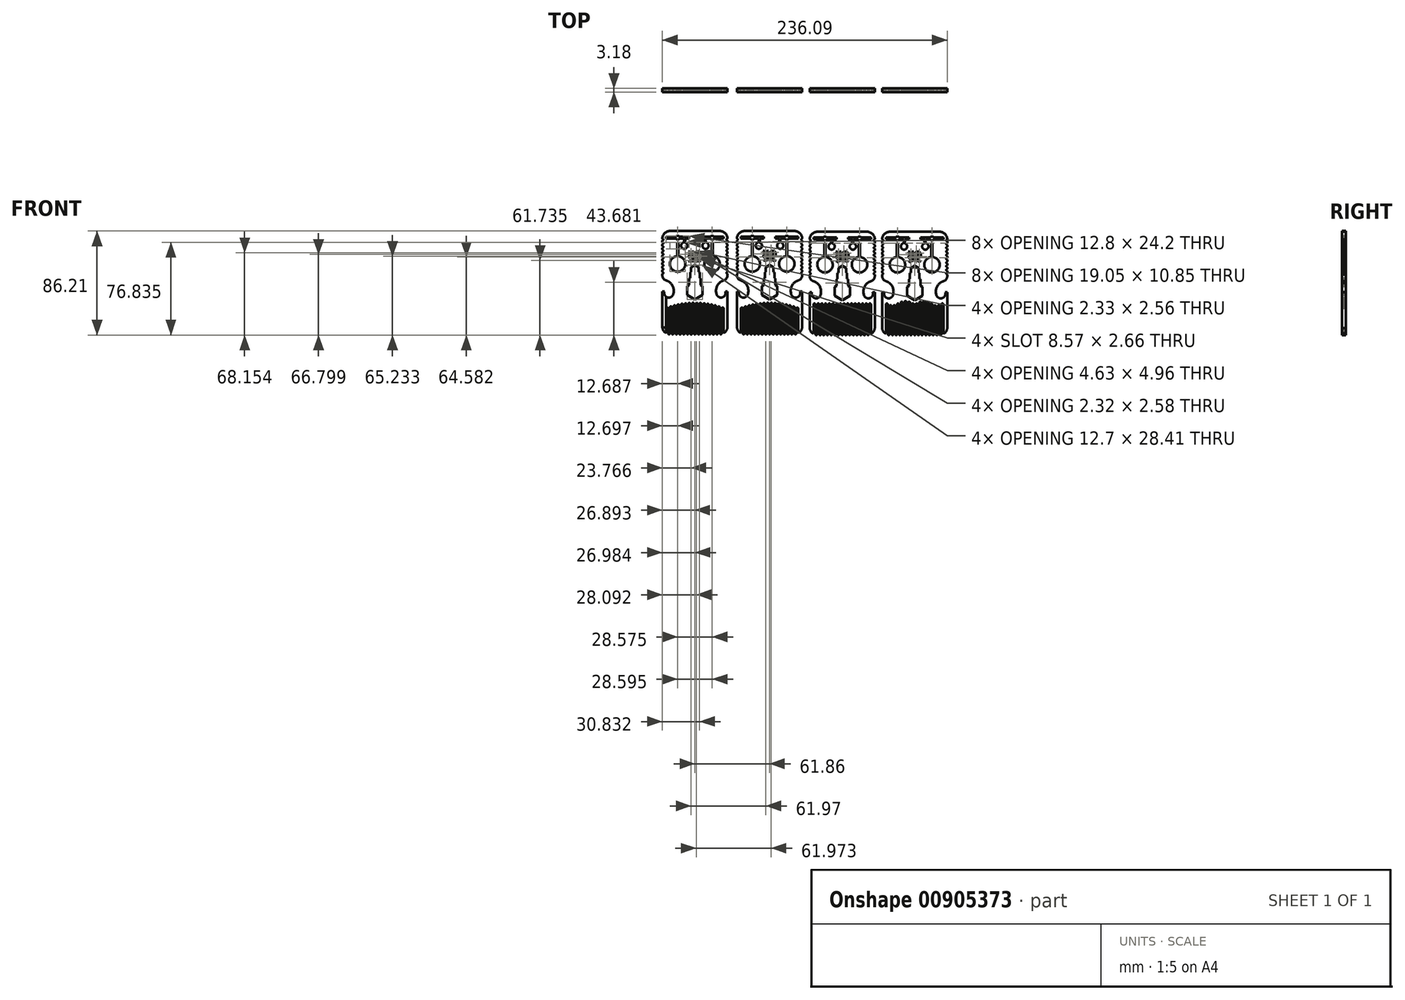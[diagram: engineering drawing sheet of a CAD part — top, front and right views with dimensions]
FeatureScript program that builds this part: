
annotation { "Feature Type Name" : "Feature", "Feature Type Description" : "" }
export const myFeature = defineFeature(function(context is Context, id is Id, definition is map)
    precondition{}
    {
        {
            var Q0;
            Q0=qCreatedBy(makeId("Front.planeOp"),FACE);
            var sketch = newSketch(context, id + "F0", { "sketchPlane" : qUnion([Q0])});
            skLineSegment(sketch, "E0.0", {"start": v(6.35, -8.3) * mm, "end": v(0, -11.96) * mm});
            skLineSegment(sketch, "E0.4", {"start": v(4.76, -0.05) * mm, "end": v(6.35, -0.97) * mm});
            skLineSegment(sketch, "E0.5", {"start": v(6.35, -0.97) * mm, "end": v(6.35, -8.3) * mm});
            skPoint(sketch, "E0.0.midPoint", {"position": v(3.17, -10.13) * mm});
            skLineSegment(sketch, "E1.4", {"start": v(3.97, 5.9) * mm, "end": v(4.76, 5.45) * mm});
            skLineSegment(sketch, "E1.5", {"start": v(4.76, 5.45) * mm, "end": v(4.76, -0.05) * mm});
            skPoint(sketch, "E2.visualSharp", {"position": v(-25.7, -41.44) * mm});
            skLineSegment(sketch, "E3.4", {"start": v(3.17, 10.95) * mm, "end": v(3.97, 10.5) * mm});
            skLineSegment(sketch, "E3.5", {"start": v(3.97, 10.5) * mm, "end": v(3.97, 5.9) * mm});
            skLineSegment(sketch, "E4.4", {"start": v(0, 16.45) * mm, "end": v(3.17, 14.61) * mm});
            skLineSegment(sketch, "E4.5", {"start": v(3.17, 14.61) * mm, "end": v(3.17, 10.95) * mm});
            skLineSegment(sketch, "E5.left", {"start": v(-26.99, 36.9) * mm, "end": v(-26.99, 35.36) * mm});
            skArc(sketch, "E6.filletArc", {"start": v(-20.64, 44.77) * mm, "mid": v(-25.13, 42.91) * mm, "end": v(-26.99, 38.42) * mm});
            skArc(sketch, "E7.filletArc", {"start": v(-26.95, -35.14) * mm, "mid": v(-26.28, -37.4) * mm, "end": v(-24.83, -39.24) * mm});
            skLineSegment(sketch, "E8", {"start": v(-23.81, 38.42) * mm, "end": v(-23.81, 40.01) * mm});
            skLineSegment(sketch, "E9", {"start": v(-23.81, 40.01) * mm, "end": v(-15.89, 40.01) * mm});
            skLineSegment(sketch, "E10", {"start": v(-4.76, 40.01) * mm, "end": v(-4.76, 38.42) * mm});
            skLineSegment(sketch, "E11", {"start": v(-23.81, 38.42) * mm, "end": v(-15.68, 38.42) * mm});
            skLineSegment(sketch, "E12.MirrorCS", {"start": v(-13.53, 27.58) * mm, "end": v(-13.53, 27.57) * mm});
            skLineSegment(sketch, "E13.MirrorCS", {"start": v(-15.06, 27.58) * mm, "end": v(-15.06, 27.57) * mm});
            skLineSegment(sketch, "E14.MirrorCS", {"start": v(-13.86, 35.24) * mm, "end": v(-14.75, 35.24) * mm});
            skLineSegment(sketch, "E15", {"start": v(-13.54, 23.8) * mm, "end": v(-13.53, 23.8) * mm});
            skLineSegment(sketch, "E16.0", {"start": v(-14.75, 35.24) * mm, "end": v(-14.75, 24.42) * mm});
            skLineSegment(sketch, "E17.0", {"start": v(-13.86, 35.24) * mm, "end": v(-13.86, 24.42) * mm});
            skArc(sketch, "E18", {"start": v(-15.3, 23.8) * mm, "mid": v(-14.28, 11.04) * mm, "end": v(-13.32, 23.8) * mm});
            skArc(sketch, "E19", {"start": v(-26.99, 9.3) * mm, "mid": v(-26.23, 10.07) * mm, "end": v(-26.99, 10.83) * mm});
            skArc(sketch, "E20", {"start": v(-26.99, 12.37) * mm, "mid": v(-26.23, 13.13) * mm, "end": v(-26.99, 13.9) * mm});
            skArc(sketch, "E21", {"start": v(-26.99, 15.43) * mm, "mid": v(-26.23, 16.2) * mm, "end": v(-26.99, 16.96) * mm});
            skArc(sketch, "E22", {"start": v(-26.99, 18.5) * mm, "mid": v(-26.23, 19.26) * mm, "end": v(-26.99, 20.03) * mm});
            skArc(sketch, "E23", {"start": v(-26.99, 21.56) * mm, "mid": v(-26.23, 22.33) * mm, "end": v(-26.99, 23.1) * mm});
            skArc(sketch, "E24", {"start": v(-26.99, 24.63) * mm, "mid": v(-26.23, 25.4) * mm, "end": v(-26.99, 26.16) * mm});
            skArc(sketch, "E25", {"start": v(-26.99, 27.7) * mm, "mid": v(-26.23, 28.46) * mm, "end": v(-26.99, 29.23) * mm});
            skArc(sketch, "E26", {"start": v(-26.99, 30.76) * mm, "mid": v(-26.23, 31.53) * mm, "end": v(-26.99, 32.3) * mm});
            skArc(sketch, "E27", {"start": v(-26.99, 33.83) * mm, "mid": v(-26.23, 34.6) * mm, "end": v(-26.99, 35.36) * mm});
            skArc(sketch, "E28", {"start": v(-26.99, 36.9) * mm, "mid": v(-26.23, 37.66) * mm, "end": v(-26.99, 38.42) * mm});
            skLineSegment(sketch, "E29.trimOffspring", {"start": v(-26.99, 12.37) * mm, "end": v(-26.99, 10.83) * mm});
            skLineSegment(sketch, "E30.trimOffspring", {"start": v(-26.99, 15.43) * mm, "end": v(-26.99, 13.9) * mm});
            skLineSegment(sketch, "E31.trimOffspring", {"start": v(-26.99, 18.5) * mm, "end": v(-26.99, 16.96) * mm});
            skLineSegment(sketch, "E32.trimOffspring", {"start": v(-26.99, 21.56) * mm, "end": v(-26.99, 20.03) * mm});
            skLineSegment(sketch, "E33.trimOffspring", {"start": v(-26.99, 24.63) * mm, "end": v(-26.99, 23.1) * mm});
            skLineSegment(sketch, "E34.trimOffspring", {"start": v(-26.99, 27.7) * mm, "end": v(-26.99, 26.16) * mm});
            skLineSegment(sketch, "E35.trimOffspring", {"start": v(-26.99, 30.76) * mm, "end": v(-26.99, 29.23) * mm});
            skLineSegment(sketch, "E36.trimOffspring", {"start": v(-26.99, 33.83) * mm, "end": v(-26.99, 32.3) * mm});
            skPoint(sketch, "E37.orphan", {"position": v(-14.3, 35.24) * mm});
            skLineSegment(sketch, "E38.trimOffspring", {"start": v(-12.71, 40.01) * mm, "end": v(-4.76, 40.01) * mm});
            skLineSegment(sketch, "E39", {"start": v(-15.89, 40.01) * mm, "end": v(-15.68, 40.01) * mm});
            skArc(sketch, "E40.MirrorCS", {"start": v(-15.68, 40.01) * mm, "mid": v(-14.29, 40.82) * mm, "end": v(-12.9, 40.01) * mm});
            skArc(sketch, "E41.MirrorCS", {"start": v(-12.9, 38.42) * mm, "mid": v(-14.29, 37.62) * mm, "end": v(-15.68, 38.42) * mm});
            skLineSegment(sketch, "E42.trimOffspring", {"start": v(-12.9, 38.42) * mm, "end": v(-9.28, 38.42) * mm});
            skLineSegment(sketch, "E43.trimOffspring", {"start": v(-12.9, 40.01) * mm, "end": v(-12.71, 40.01) * mm});
            skLineSegment(sketch, "E44.trimOffspring", {"start": v(-8.29, 38.42) * mm, "end": v(-4.76, 38.42) * mm});
            skArc(sketch, "E45", {"start": v(-9.9, 35.02) * mm, "mid": v(-8.95, 36.6) * mm, "end": v(-9.28, 38.42) * mm});
            skArc(sketch, "E46.0", {"start": v(-8.4, 35.5) * mm, "mid": v(-8.02, 36.95) * mm, "end": v(-8.29, 38.42) * mm});
            skPoint(sketch, "E47.start.orphan", {"position": v(-9.9, 35.02) * mm});
            skArc(sketch, "E48.MirrorCS", {"start": v(-9.9, 35.02) * mm, "mid": v(-8.58, 29.97) * mm, "end": v(-8.25, 35.18) * mm});
            skPoint(sketch, "E49.orphan", {"position": v(-9.94, 35) * mm});
            skArc(sketch, "E50", {"start": v(-15.3, 23.8) * mm, "mid": v(-14.92, 24.01) * mm, "end": v(-14.75, 24.42) * mm});
            skArc(sketch, "E51.MirrorCS", {"start": v(-13.3, 23.8) * mm, "mid": v(-13.69, 24.01) * mm, "end": v(-13.86, 24.42) * mm});
            skArc(sketch, "E52", {"start": v(-8.4, 35.5) * mm, "mid": v(-8.4, 35.3) * mm, "end": v(-8.25, 35.18) * mm});
            skLineSegment(sketch, "E53", {"start": v(-0.77, -40.07) * mm, "end": v(-0.77, -15.43) * mm});
            skArc(sketch, "E54", {"start": v(-0.77, -15.43) * mm, "mid": v(-1.53, -14.67) * mm, "end": v(-2.3, -15.43) * mm});
            skLineSegment(sketch, "E55", {"start": v(-2.3, -15.43) * mm, "end": v(-2.3, -40.07) * mm});
            skArc(sketch, "E56", {"start": v(-3.83, -40.07) * mm, "mid": v(-3.07, -40.82) * mm, "end": v(-2.3, -40.07) * mm});
            skLineSegment(sketch, "E57", {"start": v(-3.83, -40.07) * mm, "end": v(-3.83, -15.43) * mm});
            skArc(sketch, "E58", {"start": v(-3.83, -15.43) * mm, "mid": v(-4.6, -14.67) * mm, "end": v(-5.37, -15.43) * mm});
            skLineSegment(sketch, "E59", {"start": v(-5.37, -15.43) * mm, "end": v(-5.37, -40.07) * mm});
            skLineSegment(sketch, "E60", {"start": v(-6.9, -40.07) * mm, "end": v(-6.9, -15.43) * mm});
            skArc(sketch, "E61", {"start": v(-6.9, -15.43) * mm, "mid": v(-7.66, -14.67) * mm, "end": v(-8.43, -15.43) * mm});
            skLineSegment(sketch, "E62", {"start": v(-8.43, -15.43) * mm, "end": v(-8.43, -40.07) * mm});
            skArc(sketch, "E63", {"start": v(-6.9, -40.07) * mm, "mid": v(-6.13, -40.82) * mm, "end": v(-5.37, -40.07) * mm});
            skArc(sketch, "E64", {"start": v(-9.96, -40.07) * mm, "mid": v(-9.2, -40.82) * mm, "end": v(-8.43, -40.07) * mm});
            skLineSegment(sketch, "E65", {"start": v(-9.96, -40.07) * mm, "end": v(-9.96, -15.43) * mm});
            skArc(sketch, "E66", {"start": v(-9.96, -15.43) * mm, "mid": v(-10.73, -14.67) * mm, "end": v(-11.5, -15.43) * mm});
            skLineSegment(sketch, "E67", {"start": v(-11.5, -15.43) * mm, "end": v(-11.5, -40.07) * mm});
            skArc(sketch, "E68", {"start": v(-13.03, -40.07) * mm, "mid": v(-12.26, -40.82) * mm, "end": v(-11.5, -40.07) * mm});
            skLineSegment(sketch, "E69", {"start": v(-13.03, -40.07) * mm, "end": v(-13.03, -15.43) * mm});
            skArc(sketch, "E70", {"start": v(-13.03, -15.43) * mm, "mid": v(-13.8, -14.67) * mm, "end": v(-14.56, -15.43) * mm});
            skLineSegment(sketch, "E71", {"start": v(-14.56, -15.43) * mm, "end": v(-14.56, -40.07) * mm});
            skArc(sketch, "E72", {"start": v(-16.1, -40.07) * mm, "mid": v(-15.33, -40.82) * mm, "end": v(-14.56, -40.07) * mm});
            skLineSegment(sketch, "E73", {"start": v(-16.1, -40.07) * mm, "end": v(-16.1, -15.43) * mm});
            skArc(sketch, "E74", {"start": v(-16.1, -15.43) * mm, "mid": v(-16.86, -14.67) * mm, "end": v(-17.63, -15.43) * mm});
            skLineSegment(sketch, "E75", {"start": v(-17.63, -15.43) * mm, "end": v(-17.63, -40.07) * mm});
            skArc(sketch, "E76", {"start": v(-19.16, -40.07) * mm, "mid": v(-18.4, -40.82) * mm, "end": v(-17.63, -40.07) * mm});
            skLineSegment(sketch, "E77", {"start": v(-19.16, -40.07) * mm, "end": v(-19.16, -15.43) * mm});
            skArc(sketch, "E78", {"start": v(-19.16, -15.43) * mm, "mid": v(-19.93, -14.67) * mm, "end": v(-20.7, -15.43) * mm});
            skLineSegment(sketch, "E79", {"start": v(-20.7, -15.43) * mm, "end": v(-20.7, -40.02) * mm});
            skArc(sketch, "E80", {"start": v(-22.23, -40.01) * mm, "mid": v(-21.46, -40.77) * mm, "end": v(-20.7, -40.01) * mm});
            skLineSegment(sketch, "E81", {"start": v(-22.23, -40.01) * mm, "end": v(-22.23, -15.43) * mm});
            skArc(sketch, "E82", {"start": v(-22.23, -15.43) * mm, "mid": v(-23, -14.67) * mm, "end": v(-23.76, -15.43) * mm});
            skLineSegment(sketch, "E83", {"start": v(-23.76, -15.43) * mm, "end": v(-23.76, -38.74) * mm});
            skArc(sketch, "E84", {"start": v(-23.99, -39.27) * mm, "mid": v(-23.82, -39.03) * mm, "end": v(-23.76, -38.74) * mm});
            skArc(sketch, "E85", {"start": v(-0.77, -40.07) * mm, "mid": v(0, -40.82) * mm, "end": v(0.77, -40.07) * mm});
            skArc(sketch, "E86", {"start": v(2.3, -15.43) * mm, "mid": v(1.53, -14.67) * mm, "end": v(0.77, -15.43) * mm});
            skLineSegment(sketch, "E87.trimOffspring", {"start": v(-23.76, -40) * mm, "end": v(-23.76, -40.07) * mm});
            skArc(sketch, "E88", {"start": v(-24.83, -39.24) * mm, "mid": v(-24.41, -39.4) * mm, "end": v(-23.99, -39.27) * mm});
            skArc(sketch, "E89.MirrorCS", {"start": v(-26.98, 7.98) * mm, "mid": v(-26.1, 5.37) * mm, "end": v(-23.85, 3.81) * mm});
            skArc(sketch, "E90.MirrorCS", {"start": v(-20.94, 2.36) * mm, "mid": v(-22.34, 3.19) * mm, "end": v(-23.85, 3.81) * mm});
            skArc(sketch, "E91.MirrorCS", {"start": v(-17.92, -7.48) * mm, "mid": v(-17.94, -2.1) * mm, "end": v(-20.94, 2.36) * mm});
            skArc(sketch, "E92.MirrorCS", {"start": v(-25.18, -5.22) * mm, "mid": v(-22.75, -10.22) * mm, "end": v(-17.92, -7.48) * mm});
            skLineSegment(sketch, "E93.MirrorCS", {"start": v(-25.18, -5.22) * mm, "end": v(-26.98, -5.22) * mm});
            skLineSegment(sketch, "E94.MirrorCS", {"start": v(-26.98, -5.22) * mm, "end": v(-26.95, -35.14) * mm});
            skLineSegment(sketch, "E95", {"start": v(-26.98, 7.98) * mm, "end": v(-26.99, 9.3) * mm});
            skArc(sketch, "E96.MirrorCS", {"start": v(20.64, 44.77) * mm, "mid": v(25.13, 42.91) * mm, "end": v(26.99, 38.42) * mm});
            skLineSegment(sketch, "E97.MirrorCS", {"start": v(23.81, 40.01) * mm, "end": v(15.89, 40.01) * mm});
            skArc(sketch, "E98.MirrorCS", {"start": v(15.68, 40.01) * mm, "mid": v(14.29, 40.82) * mm, "end": v(12.9, 40.01) * mm});
            skLineSegment(sketch, "E99.MirrorCS", {"start": v(12.71, 40.01) * mm, "end": v(4.76, 40.01) * mm});
            skLineSegment(sketch, "E100.MirrorCS", {"start": v(4.76, 40.01) * mm, "end": v(4.76, 38.42) * mm});
            skLineSegment(sketch, "E101.MirrorCS", {"start": v(8.29, 38.42) * mm, "end": v(4.76, 38.42) * mm});
            skArc(sketch, "E102.MirrorCS", {"start": v(8.4, 35.5) * mm, "mid": v(8.02, 36.95) * mm, "end": v(8.29, 38.42) * mm});
            skLineSegment(sketch, "E103.MirrorCS", {"start": v(13.86, 35.24) * mm, "end": v(13.86, 24.42) * mm});
            skLineSegment(sketch, "E104.MirrorCS", {"start": v(14.75, 35.24) * mm, "end": v(14.75, 24.42) * mm});
            skLineSegment(sketch, "E105.MirrorCS", {"start": v(13.86, 35.24) * mm, "end": v(14.75, 35.24) * mm});
            skLineSegment(sketch, "E106.MirrorCS", {"start": v(12.9, 38.42) * mm, "end": v(9.28, 38.42) * mm});
            skArc(sketch, "E107.MirrorCS", {"start": v(12.9, 38.42) * mm, "mid": v(14.29, 37.62) * mm, "end": v(15.68, 38.42) * mm});
            skLineSegment(sketch, "E108.MirrorCS", {"start": v(23.81, 38.42) * mm, "end": v(15.68, 38.42) * mm});
            skLineSegment(sketch, "E109.MirrorCS", {"start": v(23.81, 38.42) * mm, "end": v(23.81, 40.01) * mm});
            skArc(sketch, "E110.MirrorCS", {"start": v(9.9, 35.02) * mm, "mid": v(8.95, 36.6) * mm, "end": v(9.28, 38.42) * mm});
            skArc(sketch, "E111.MirrorCS", {"start": v(9.9, 35.02) * mm, "mid": v(8.58, 29.97) * mm, "end": v(8.25, 35.18) * mm});
            skArc(sketch, "E112.MirrorCS", {"start": v(8.4, 35.5) * mm, "mid": v(8.4, 35.3) * mm, "end": v(8.25, 35.18) * mm});
            skLineSegment(sketch, "E113.MirrorCS", {"start": v(26.98, 7.98) * mm, "end": v(26.99, 9.3) * mm});
            skArc(sketch, "E114.MirrorCS", {"start": v(26.99, 33.83) * mm, "mid": v(26.23, 34.6) * mm, "end": v(26.99, 35.36) * mm});
            skLineSegment(sketch, "E115.MirrorCS", {"start": v(26.99, 33.83) * mm, "end": v(26.99, 32.3) * mm});
            skArc(sketch, "E116.MirrorCS", {"start": v(26.99, 9.3) * mm, "mid": v(26.23, 10.07) * mm, "end": v(26.99, 10.83) * mm});
            skArc(sketch, "E117.MirrorCS", {"start": v(26.99, 27.7) * mm, "mid": v(26.23, 28.46) * mm, "end": v(26.99, 29.23) * mm});
            skLineSegment(sketch, "E118.MirrorCS", {"start": v(26.99, 36.9) * mm, "end": v(26.99, 35.36) * mm});
            skLineSegment(sketch, "E119.MirrorCS", {"start": v(26.99, 15.43) * mm, "end": v(26.99, 13.9) * mm});
            skLineSegment(sketch, "E120.MirrorCS", {"start": v(26.99, 24.63) * mm, "end": v(26.99, 23.1) * mm});
            skLineSegment(sketch, "E121.MirrorCS", {"start": v(26.99, 21.56) * mm, "end": v(26.99, 20.03) * mm});
            skLineSegment(sketch, "E122.MirrorCS", {"start": v(26.99, 18.5) * mm, "end": v(26.99, 16.96) * mm});
            skArc(sketch, "E123.MirrorCS", {"start": v(26.99, 30.76) * mm, "mid": v(26.23, 31.53) * mm, "end": v(26.99, 32.3) * mm});
            skArc(sketch, "E124.MirrorCS", {"start": v(26.99, 21.56) * mm, "mid": v(26.23, 22.33) * mm, "end": v(26.99, 23.1) * mm});
            skLineSegment(sketch, "E125.MirrorCS", {"start": v(26.99, 30.76) * mm, "end": v(26.99, 29.23) * mm});
            skArc(sketch, "E126.MirrorCS", {"start": v(26.99, 24.63) * mm, "mid": v(26.23, 25.4) * mm, "end": v(26.99, 26.16) * mm});
            skArc(sketch, "E127.MirrorCS", {"start": v(26.99, 36.9) * mm, "mid": v(26.23, 37.66) * mm, "end": v(26.99, 38.42) * mm});
            skLineSegment(sketch, "E128.MirrorCS", {"start": v(26.99, 12.37) * mm, "end": v(26.99, 10.83) * mm});
            skLineSegment(sketch, "E129.MirrorCS", {"start": v(26.99, 27.7) * mm, "end": v(26.99, 26.16) * mm});
            skArc(sketch, "E130.MirrorCS", {"start": v(26.99, 15.43) * mm, "mid": v(26.23, 16.2) * mm, "end": v(26.99, 16.96) * mm});
            skArc(sketch, "E131.MirrorCS", {"start": v(26.99, 12.37) * mm, "mid": v(26.23, 13.13) * mm, "end": v(26.99, 13.9) * mm});
            skArc(sketch, "E132.MirrorCS", {"start": v(26.99, 18.5) * mm, "mid": v(26.23, 19.26) * mm, "end": v(26.99, 20.03) * mm});
            skArc(sketch, "E133.MirrorCS", {"start": v(13.03, -40.07) * mm, "mid": v(12.26, -40.82) * mm, "end": v(11.5, -40.07) * mm});
            skArc(sketch, "E134.MirrorCS", {"start": v(19.16, -40.07) * mm, "mid": v(18.4, -40.82) * mm, "end": v(17.63, -40.07) * mm});
            skArc(sketch, "E135.MirrorCS", {"start": v(9.96, -40.07) * mm, "mid": v(9.2, -40.82) * mm, "end": v(8.43, -40.07) * mm});
            skArc(sketch, "E136.MirrorCS", {"start": v(6.9, -40.07) * mm, "mid": v(6.13, -40.82) * mm, "end": v(5.37, -40.07) * mm});
            skLineSegment(sketch, "E137.MirrorCS", {"start": v(13.54, 23.8) * mm, "end": v(13.53, 23.8) * mm});
            skArc(sketch, "E138.MirrorCS", {"start": v(0.77, -40.07) * mm, "mid": v(0, -40.82) * mm, "end": v(-0.77, -40.07) * mm});
            skArc(sketch, "E139.MirrorCS", {"start": v(0.77, -15.43) * mm, "mid": v(1.53, -14.67) * mm, "end": v(2.3, -15.43) * mm});
            skArc(sketch, "E140.MirrorCS", {"start": v(13.3, 23.8) * mm, "mid": v(13.69, 24.01) * mm, "end": v(13.86, 24.42) * mm});
            skArc(sketch, "E141.MirrorCS", {"start": v(15.3, 23.8) * mm, "mid": v(14.92, 24.01) * mm, "end": v(14.75, 24.42) * mm});
            skLineSegment(sketch, "E142.MirrorCS", {"start": v(23.76, -40) * mm, "end": v(23.76, -40.07) * mm});
            skArc(sketch, "E143.MirrorCS", {"start": v(22.23, -40.01) * mm, "mid": v(21.46, -40.77) * mm, "end": v(20.7, -40.01) * mm});
            skLineSegment(sketch, "E144.MirrorCS", {"start": v(12.9, 40.01) * mm, "end": v(12.71, 40.01) * mm});
            skArc(sketch, "E145.MirrorCS", {"start": v(3.83, -40.07) * mm, "mid": v(3.07, -40.82) * mm, "end": v(2.3, -40.07) * mm});
            skLineSegment(sketch, "E146.MirrorCS", {"start": v(15.89, 40.01) * mm, "end": v(15.68, 40.01) * mm});
            skArc(sketch, "E147.MirrorCS", {"start": v(16.1, -40.07) * mm, "mid": v(15.33, -40.82) * mm, "end": v(14.56, -40.07) * mm});
            skArc(sketch, "E148.MirrorCS", {"start": v(24.83, -39.24) * mm, "mid": v(24.41, -39.4) * mm, "end": v(23.99, -39.27) * mm});
            skLineSegment(sketch, "E149.MirrorCS", {"start": v(25.18, -5.22) * mm, "end": v(26.98, -5.22) * mm});
            skArc(sketch, "E150.MirrorCS", {"start": v(26.95, -35.14) * mm, "mid": v(26.28, -37.4) * mm, "end": v(24.83, -39.24) * mm});
            skLineSegment(sketch, "E151.MirrorCS", {"start": v(-3.18, 10.95) * mm, "end": v(-3.97, 10.5) * mm});
            skArc(sketch, "E152.MirrorCS", {"start": v(23.99, -39.27) * mm, "mid": v(23.82, -39.03) * mm, "end": v(23.76, -38.74) * mm});
            skLineSegment(sketch, "E153.MirrorCS", {"start": v(-3.97, 10.5) * mm, "end": v(-3.97, 5.9) * mm});
            skLineSegment(sketch, "E154.MirrorCS", {"start": v(-3.18, 14.61) * mm, "end": v(-3.18, 10.95) * mm});
            skLineSegment(sketch, "E155.MirrorCS", {"start": v(-3.97, 5.9) * mm, "end": v(-4.76, 5.45) * mm});
            skLineSegment(sketch, "E156.MirrorCS", {"start": v(13.53, 27.58) * mm, "end": v(13.53, 27.57) * mm});
            skLineSegment(sketch, "E157.MirrorCS", {"start": v(15.06, 27.58) * mm, "end": v(15.06, 27.57) * mm});
            skArc(sketch, "E158.MirrorCS", {"start": v(20.94, 2.36) * mm, "mid": v(22.34, 3.19) * mm, "end": v(23.85, 3.81) * mm});
            skLineSegment(sketch, "E159.MirrorCS", {"start": v(-4.76, -0.05) * mm, "end": v(-6.35, -0.97) * mm});
            skLineSegment(sketch, "E160.MirrorCS", {"start": v(0, 16.45) * mm, "end": v(-3.18, 14.61) * mm});
            skLineSegment(sketch, "E161.MirrorCS", {"start": v(-6.35, -8.3) * mm, "end": v(0, -11.96) * mm});
            skLineSegment(sketch, "E162.MirrorCS", {"start": v(17.63, -16.84) * mm, "end": v(17.63, -40.07) * mm});
            skLineSegment(sketch, "E163.MirrorCS", {"start": v(-6.35, -0.97) * mm, "end": v(-6.35, -8.3) * mm});
            skLineSegment(sketch, "E164.MirrorCS", {"start": v(11.5, -15.43) * mm, "end": v(11.5, -40.07) * mm});
            skLineSegment(sketch, "E165.MirrorCS", {"start": v(22.23, -40.01) * mm, "end": v(22.23, -15.43) * mm});
            skLineSegment(sketch, "E166.MirrorCS", {"start": v(26.98, -5.22) * mm, "end": v(26.95, -35.14) * mm});
            skArc(sketch, "E167.MirrorCS", {"start": v(17.92, -7.48) * mm, "mid": v(17.94, -2.1) * mm, "end": v(20.94, 2.36) * mm});
            skLineSegment(sketch, "E168.MirrorCS", {"start": v(23.76, -15.43) * mm, "end": v(23.76, -38.74) * mm});
            skPoint(sketch, "E169.MirrorP", {"position": v(14.3, 35.24) * mm});
            skArc(sketch, "E170.MirrorCS", {"start": v(25.18, -5.22) * mm, "mid": v(22.75, -10.22) * mm, "end": v(17.92, -7.48) * mm});
            skLineSegment(sketch, "E171.MirrorCS", {"start": v(0.77, -40.07) * mm, "end": v(0.77, -15.43) * mm});
            skPoint(sketch, "E172.MirrorP", {"position": v(-3.18, -10.13) * mm});
            skLineSegment(sketch, "E173.MirrorCS", {"start": v(16.1, -40.07) * mm, "end": v(16.1, -16.84) * mm});
            skPoint(sketch, "E174.MirrorP", {"position": v(26.99, -34.47) * mm});
            skPoint(sketch, "E175.MirrorP", {"position": v(9.9, 35.02) * mm});
            skLineSegment(sketch, "E176.MirrorCS", {"start": v(3.83, -40.07) * mm, "end": v(3.83, -15.43) * mm});
            skLineSegment(sketch, "E177.MirrorCS", {"start": v(14.56, -15.43) * mm, "end": v(14.56, -40.07) * mm});
            skArc(sketch, "E178.MirrorCS", {"start": v(15.3, 23.8) * mm, "mid": v(14.28, 11.04) * mm, "end": v(13.32, 23.8) * mm});
            skPoint(sketch, "E179.MirrorP", {"position": v(9.94, 35) * mm});
            skArc(sketch, "E180.MirrorCS", {"start": v(26.98, 7.98) * mm, "mid": v(26.1, 5.37) * mm, "end": v(23.85, 3.81) * mm});
            skLineSegment(sketch, "E181.MirrorCS", {"start": v(5.37, -15.43) * mm, "end": v(5.37, -40.07) * mm});
            skLineSegment(sketch, "E182.MirrorCS", {"start": v(-4.76, 5.45) * mm, "end": v(-4.76, -0.05) * mm});
            skLineSegment(sketch, "E183.MirrorCS", {"start": v(13.03, -40.07) * mm, "end": v(13.03, -15.43) * mm});
            skPoint(sketch, "E184.MirrorP", {"position": v(25.7, -41.44) * mm});
            skLineSegment(sketch, "E185.MirrorCS", {"start": v(19.16, -40.07) * mm, "end": v(19.16, -16.84) * mm});
            skLineSegment(sketch, "E186.MirrorCS", {"start": v(9.96, -40.07) * mm, "end": v(9.96, -15.43) * mm});
            skLineSegment(sketch, "E187.MirrorCS", {"start": v(8.43, -15.43) * mm, "end": v(8.43, -40.07) * mm});
            skLineSegment(sketch, "E188.MirrorCS", {"start": v(2.3, -15.43) * mm, "end": v(2.3, -40.07) * mm});
            skLineSegment(sketch, "E189.MirrorCS", {"start": v(6.9, -40.07) * mm, "end": v(6.9, -15.43) * mm});
            skLineSegment(sketch, "E190", {"start": v(-20.64, 44.77) * mm, "end": v(20.64, 44.77) * mm});
            skArc(sketch, "E191", {"start": v(4.3, 20.82) * mm, "mid": v(0, 22.07) * mm, "end": v(-4.26, 20.7) * mm});
            skArc(sketch, "E192", {"start": v(1.59, 27.05) * mm, "mid": v(1.34, 26.49) * mm, "end": v(1.22, 25.88) * mm});
            skArc(sketch, "E193", {"start": v(1.32, 24.9) * mm, "mid": v(1.68, 24.22) * mm, "end": v(2.39, 23.9) * mm});
            skArc(sketch, "E194", {"start": v(2.38, 28.44) * mm, "mid": v(2.03, 28.4) * mm, "end": v(1.69, 28.32) * mm});
            skArc(sketch, "E195", {"start": v(1.69, 28.32) * mm, "mid": v(1.26, 28.15) * mm, "end": v(0.88, 27.9) * mm});
            skArc(sketch, "E196", {"start": v(0.88, 27.9) * mm, "mid": v(0.52, 27.5) * mm, "end": v(0.28, 27.03) * mm});
            skArc(sketch, "E197", {"start": v(0.28, 27.03) * mm, "mid": v(0.11, 26.47) * mm, "end": v(0.05, 25.88) * mm});
            skArc(sketch, "E198", {"start": v(0.05, 25.88) * mm, "mid": v(0.05, 25.88) * mm, "end": v(0.05, 25.88) * mm});
            skArc(sketch, "E199", {"start": v(0.09, 25.07) * mm, "mid": v(0.16, 24.69) * mm, "end": v(0.28, 24.32) * mm});
            skArc(sketch, "E200", {"start": v(0.28, 24.32) * mm, "mid": v(0.42, 24.03) * mm, "end": v(0.6, 23.76) * mm});
            skArc(sketch, "E201", {"start": v(0.6, 23.76) * mm, "mid": v(0.86, 23.5) * mm, "end": v(1.16, 23.28) * mm});
            skArc(sketch, "E202", {"start": v(1.16, 23.28) * mm, "mid": v(1.5, 23.12) * mm, "end": v(1.87, 23.02) * mm});
            skArc(sketch, "E203", {"start": v(1.87, 23.02) * mm, "mid": v(2.1, 22.97) * mm, "end": v(2.35, 22.95) * mm});
            skArc(sketch, "E204", {"start": v(2.35, 22.95) * mm, "mid": v(2.37, 22.95) * mm, "end": v(2.39, 22.95) * mm});
            skLineSegment(sketch, "E205", {"start": v(2.58, 27.5) * mm, "end": v(2.58, 27.5) * mm});
            skLineSegment(sketch, "E206", {"start": v(2.59, 23.88) * mm, "end": v(2.59, 23.87) * mm});
            skLineSegment(sketch, "E207.trimOffspring", {"start": v(2.39, 27.47) * mm, "end": v(2.38, 28.44) * mm});
            skLineSegment(sketch, "E208", {"start": v(2.39, 23.42) * mm, "end": v(2.39, 22.95) * mm});
            skArc(sketch, "E209.trimOffspring", {"start": v(2.59, 22.94) * mm, "mid": v(2.6, 22.94) * mm, "end": v(2.6, 22.94) * mm});
            skLineSegment(sketch, "E210.trimOffspring", {"start": v(2.39, 23.9) * mm, "end": v(2.39, 23.42) * mm});
            skArc(sketch, "E211.trimOffspring", {"start": v(2.39, 27.47) * mm, "mid": v(1.95, 27.33) * mm, "end": v(1.59, 27.05) * mm});
            skPoint(sketch, "E212.orphan", {"position": v(1.21, 25.62) * mm});
            skArc(sketch, "E213.MirrorCS", {"start": v(2.77, 27.48) * mm, "mid": v(3.2, 27.34) * mm, "end": v(3.57, 27.06) * mm});
            skArc(sketch, "E214.MirrorCS", {"start": v(3.57, 27.06) * mm, "mid": v(3.82, 26.5) * mm, "end": v(3.94, 25.9) * mm});
            skArc(sketch, "E215.MirrorCS", {"start": v(3.86, 24.92) * mm, "mid": v(3.5, 24.23) * mm, "end": v(2.8, 23.9) * mm});
            skArc(sketch, "E216.MirrorCS", {"start": v(2.85, 22.95) * mm, "mid": v(2.83, 22.95) * mm, "end": v(2.8, 22.95) * mm});
            skArc(sketch, "E217.MirrorCS", {"start": v(3.32, 23.02) * mm, "mid": v(3.09, 22.98) * mm, "end": v(2.85, 22.95) * mm});
            skArc(sketch, "E218.MirrorCS", {"start": v(4.03, 23.3) * mm, "mid": v(3.69, 23.13) * mm, "end": v(3.32, 23.02) * mm});
            skArc(sketch, "E219.MirrorCS", {"start": v(4.58, 23.78) * mm, "mid": v(4.33, 23.52) * mm, "end": v(4.03, 23.3) * mm});
            skArc(sketch, "E220.MirrorCS", {"start": v(4.9, 24.34) * mm, "mid": v(4.76, 24.05) * mm, "end": v(4.58, 23.78) * mm});
            skArc(sketch, "E221.MirrorCS", {"start": v(5.08, 25.1) * mm, "mid": v(5.02, 24.71) * mm, "end": v(4.9, 24.34) * mm});
            skArc(sketch, "E222.MirrorCS", {"start": v(5.11, 25.9) * mm, "mid": v(5.11, 25.9) * mm, "end": v(5.11, 25.9) * mm});
            skArc(sketch, "E223.MirrorCS", {"start": v(4.88, 27.05) * mm, "mid": v(5.05, 26.5) * mm, "end": v(5.11, 25.9) * mm});
            skArc(sketch, "E224.MirrorCS", {"start": v(4.27, 27.9) * mm, "mid": v(4.63, 27.52) * mm, "end": v(4.88, 27.05) * mm});
            skArc(sketch, "E225.MirrorCS", {"start": v(3.45, 28.33) * mm, "mid": v(3.88, 28.16) * mm, "end": v(4.27, 27.9) * mm});
            skArc(sketch, "E226.MirrorCS", {"start": v(2.76, 28.44) * mm, "mid": v(3.11, 28.4) * mm, "end": v(3.45, 28.33) * mm});
            skLineSegment(sketch, "E227.MirrorCS", {"start": v(2.77, 27.48) * mm, "end": v(2.76, 28.44) * mm});
            skLineSegment(sketch, "E228.MirrorCS", {"start": v(2.8, 23.9) * mm, "end": v(2.8, 23.42) * mm});
            skLineSegment(sketch, "E229.MirrorCS", {"start": v(2.8, 23.42) * mm, "end": v(2.8, 22.95) * mm});
            skArc(sketch, "E230", {"start": v(2.59, 23.87) * mm, "mid": v(2.6, 23.87) * mm, "end": v(2.6, 23.87) * mm});
            skLineSegment(sketch, "E231.0", {"start": v(0.05, 25.5) * mm, "end": v(1.22, 25.5) * mm});
            skLineSegment(sketch, "E232.0", {"start": v(0.05, 25.88) * mm, "end": v(1.22, 25.88) * mm});
            skLineSegment(sketch, "E233.trimOffspring", {"start": v(3.94, 25.9) * mm, "end": v(5.12, 25.9) * mm});
            skPoint(sketch, "E234.orphan", {"position": v(2.58, 25.7) * mm});
            skLineSegment(sketch, "E235.trimOffspring", {"start": v(3.95, 25.52) * mm, "end": v(5.12, 25.53) * mm});
            skPoint(sketch, "E236.MirrorCS.end.orphan", {"position": v(2.6, 23.87) * mm});
            skPoint(sketch, "E236.MirrorCS.start.orphan", {"position": v(2.8, 23.9) * mm});
            skPoint(sketch, "E237.MirrorCS.end.orphan", {"position": v(2.98, 22.94) * mm});
            skPoint(sketch, "E237.MirrorCS.start.orphan", {"position": v(3.19, 22.95) * mm});
            skPoint(sketch, "E238.orphan", {"position": v(2.57, 28.44) * mm});
            skPoint(sketch, "E239.MirrorCS.end.orphan", {"position": v(2.77, 27.48) * mm});
            skArc(sketch, "E240.trimOffspring", {"start": v(0.05, 25.5) * mm, "mid": v(0.06, 25.29) * mm, "end": v(0.09, 25.07) * mm});
            skArc(sketch, "E241.trimOffspring", {"start": v(1.22, 25.5) * mm, "mid": v(1.25, 25.2) * mm, "end": v(1.32, 24.9) * mm});
            skArc(sketch, "E242.trimOffspring", {"start": v(3.95, 25.52) * mm, "mid": v(3.92, 25.22) * mm, "end": v(3.86, 24.92) * mm});
            skArc(sketch, "E243.trimOffspring", {"start": v(5.12, 25.53) * mm, "mid": v(5.1, 25.31) * mm, "end": v(5.08, 25.1) * mm});
            skText(sketch, "E244", { "text": "X", "fontName": "OpenSans-Bold.ttf"});
            skLineSegment(sketch, "E245", {"start": v(4.3, 19.56) * mm, "end": v(4.3, 20.82) * mm});
            skLineSegment(sketch, "E246", {"start": v(4.3, 20.82) * mm, "end": v(4.3, 19.56) * mm});
            skCircle(sketch, "E247", {"center": v(2.58, 25.7) * mm, "radius": 0.65 * mm});
            skArc(sketch, "E248.0", {"start": v(4.3, 19.56) * mm, "mid": v(0, 21.05) * mm, "end": v(-4.26, 19.4) * mm});
            skLineSegment(sketch, "E249", {"start": v(-4.26, 20.7) * mm, "end": v(-4.26, 19.4) * mm});
            skLineSegment(sketch, "E250.trimOffspring", {"start": v(20.7, -16.84) * mm, "end": v(20.7, -40.02) * mm});
            skLineSegment(sketch, "E251.0", {"start": v(66.38, -8.3) * mm, "end": v(60.03, -11.96) * mm});
            skLineSegment(sketch, "E251.4", {"start": v(64.8, -0.05) * mm, "end": v(66.38, -0.97) * mm});
            skLineSegment(sketch, "E251.5", {"start": v(66.38, -0.97) * mm, "end": v(66.38, -8.3) * mm});
            skPoint(sketch, "E251.0.midPoint", {"position": v(63.2, -10.13) * mm});
            skLineSegment(sketch, "E252.4", {"start": v(64, 5.9) * mm, "end": v(64.8, 5.45) * mm});
            skLineSegment(sketch, "E252.5", {"start": v(64.8, 5.45) * mm, "end": v(64.8, -0.05) * mm});
            skPoint(sketch, "E253.visualSharp", {"position": v(34.33, -41.44) * mm});
            skLineSegment(sketch, "E254.4", {"start": v(63.2, 10.95) * mm, "end": v(64, 10.5) * mm});
            skLineSegment(sketch, "E254.5", {"start": v(64, 10.5) * mm, "end": v(64, 5.9) * mm});
            skLineSegment(sketch, "E255.4", {"start": v(60.03, 16.45) * mm, "end": v(63.2, 14.61) * mm});
            skLineSegment(sketch, "E255.5", {"start": v(63.2, 14.61) * mm, "end": v(63.2, 10.95) * mm});
            skLineSegment(sketch, "E256.left", {"start": v(33.04, 36.9) * mm, "end": v(33.04, 35.36) * mm});
            skArc(sketch, "E257.filletArc", {"start": v(39.4, 44.77) * mm, "mid": v(34.9, 42.91) * mm, "end": v(33.04, 38.42) * mm});
            skArc(sketch, "E258.filletArc", {"start": v(33.08, -35.14) * mm, "mid": v(33.75, -37.4) * mm, "end": v(35.2, -39.24) * mm});
            skLineSegment(sketch, "E259", {"start": v(36.22, 38.42) * mm, "end": v(36.22, 40.01) * mm});
            skLineSegment(sketch, "E260", {"start": v(36.22, 40.01) * mm, "end": v(44.14, 40.01) * mm});
            skLineSegment(sketch, "E261", {"start": v(55.27, 40.01) * mm, "end": v(55.27, 38.42) * mm});
            skLineSegment(sketch, "E262", {"start": v(36.22, 38.42) * mm, "end": v(44.35, 38.42) * mm});
            skLineSegment(sketch, "E263.MirrorCS", {"start": v(46.5, 27.58) * mm, "end": v(46.5, 27.57) * mm});
            skLineSegment(sketch, "E264.MirrorCS", {"start": v(44.97, 27.58) * mm, "end": v(44.97, 27.57) * mm});
            skLineSegment(sketch, "E265.MirrorCS", {"start": v(46.17, 35.24) * mm, "end": v(45.28, 35.24) * mm});
            skLineSegment(sketch, "E266", {"start": v(46.49, 23.8) * mm, "end": v(46.5, 23.8) * mm});
            skLineSegment(sketch, "E267.0", {"start": v(45.28, 35.24) * mm, "end": v(45.28, 24.42) * mm});
            skLineSegment(sketch, "E268.0", {"start": v(46.17, 35.24) * mm, "end": v(46.17, 24.42) * mm});
            skArc(sketch, "E269", {"start": v(44.73, 23.8) * mm, "mid": v(45.75, 11.04) * mm, "end": v(46.71, 23.8) * mm});
            skArc(sketch, "E270", {"start": v(33.04, 9.3) * mm, "mid": v(33.8, 10.07) * mm, "end": v(33.04, 10.83) * mm});
            skArc(sketch, "E271", {"start": v(33.04, 12.37) * mm, "mid": v(33.8, 13.13) * mm, "end": v(33.04, 13.9) * mm});
            skArc(sketch, "E272", {"start": v(33.04, 15.43) * mm, "mid": v(33.8, 16.2) * mm, "end": v(33.04, 16.96) * mm});
            skArc(sketch, "E273", {"start": v(33.04, 18.5) * mm, "mid": v(33.8, 19.26) * mm, "end": v(33.04, 20.03) * mm});
            skArc(sketch, "E274", {"start": v(33.04, 21.56) * mm, "mid": v(33.8, 22.33) * mm, "end": v(33.04, 23.1) * mm});
            skArc(sketch, "E275", {"start": v(33.04, 24.63) * mm, "mid": v(33.8, 25.4) * mm, "end": v(33.04, 26.16) * mm});
            skArc(sketch, "E276", {"start": v(33.04, 27.7) * mm, "mid": v(33.8, 28.46) * mm, "end": v(33.04, 29.23) * mm});
            skArc(sketch, "E277", {"start": v(33.04, 30.76) * mm, "mid": v(33.8, 31.53) * mm, "end": v(33.04, 32.3) * mm});
            skArc(sketch, "E278", {"start": v(33.04, 33.83) * mm, "mid": v(33.8, 34.6) * mm, "end": v(33.04, 35.36) * mm});
            skArc(sketch, "E279", {"start": v(33.04, 36.9) * mm, "mid": v(33.8, 37.66) * mm, "end": v(33.04, 38.42) * mm});
            skLineSegment(sketch, "E280.trimOffspring", {"start": v(33.04, 12.37) * mm, "end": v(33.04, 10.83) * mm});
            skLineSegment(sketch, "E281.trimOffspring", {"start": v(33.04, 15.43) * mm, "end": v(33.04, 13.9) * mm});
            skLineSegment(sketch, "E282.trimOffspring", {"start": v(33.04, 18.5) * mm, "end": v(33.04, 16.96) * mm});
            skLineSegment(sketch, "E283.trimOffspring", {"start": v(33.04, 21.56) * mm, "end": v(33.04, 20.03) * mm});
            skLineSegment(sketch, "E284.trimOffspring", {"start": v(33.04, 24.63) * mm, "end": v(33.04, 23.1) * mm});
            skLineSegment(sketch, "E285.trimOffspring", {"start": v(33.04, 27.7) * mm, "end": v(33.04, 26.16) * mm});
            skLineSegment(sketch, "E286.trimOffspring", {"start": v(33.04, 30.76) * mm, "end": v(33.04, 29.23) * mm});
            skLineSegment(sketch, "E287.trimOffspring", {"start": v(33.04, 33.83) * mm, "end": v(33.04, 32.3) * mm});
            skPoint(sketch, "E288.orphan", {"position": v(45.73, 35.24) * mm});
            skLineSegment(sketch, "E289.trimOffspring", {"start": v(47.32, 40.01) * mm, "end": v(55.27, 40.01) * mm});
            skLineSegment(sketch, "E290", {"start": v(44.14, 40.01) * mm, "end": v(44.35, 40.01) * mm});
            skArc(sketch, "E291.MirrorCS", {"start": v(44.35, 40.01) * mm, "mid": v(45.74, 40.82) * mm, "end": v(47.13, 40.01) * mm});
            skArc(sketch, "E292.MirrorCS", {"start": v(47.13, 38.42) * mm, "mid": v(45.74, 37.62) * mm, "end": v(44.35, 38.42) * mm});
            skLineSegment(sketch, "E293.trimOffspring", {"start": v(47.13, 38.42) * mm, "end": v(50.75, 38.42) * mm});
            skLineSegment(sketch, "E294.trimOffspring", {"start": v(47.13, 40.01) * mm, "end": v(47.32, 40.01) * mm});
            skLineSegment(sketch, "E295.trimOffspring", {"start": v(51.74, 38.42) * mm, "end": v(55.27, 38.42) * mm});
            skArc(sketch, "E296", {"start": v(50.12, 35.02) * mm, "mid": v(51.08, 36.6) * mm, "end": v(50.75, 38.42) * mm});
            skArc(sketch, "E297.0", {"start": v(51.63, 35.5) * mm, "mid": v(52, 36.95) * mm, "end": v(51.74, 38.42) * mm});
            skPoint(sketch, "E298.start.orphan", {"position": v(50.12, 35.02) * mm});
            skArc(sketch, "E299.MirrorCS", {"start": v(50.12, 35.02) * mm, "mid": v(51.45, 29.97) * mm, "end": v(51.78, 35.18) * mm});
            skPoint(sketch, "E300.orphan", {"position": v(50.1, 35) * mm});
            skArc(sketch, "E301", {"start": v(44.73, 23.8) * mm, "mid": v(45.11, 24.01) * mm, "end": v(45.28, 24.42) * mm});
            skArc(sketch, "E302.MirrorCS", {"start": v(46.73, 23.8) * mm, "mid": v(46.35, 24.01) * mm, "end": v(46.17, 24.42) * mm});
            skArc(sketch, "E303", {"start": v(51.63, 35.5) * mm, "mid": v(51.64, 35.3) * mm, "end": v(51.78, 35.18) * mm});
            skLineSegment(sketch, "E304", {"start": v(59.26, -40.07) * mm, "end": v(59.26, -15.43) * mm});
            skArc(sketch, "E305", {"start": v(59.26, -15.43) * mm, "mid": v(58.5, -14.67) * mm, "end": v(57.73, -15.43) * mm});
            skLineSegment(sketch, "E306", {"start": v(57.73, -15.43) * mm, "end": v(57.73, -40.07) * mm});
            skArc(sketch, "E307", {"start": v(56.2, -40.07) * mm, "mid": v(56.97, -40.82) * mm, "end": v(57.73, -40.07) * mm});
            skLineSegment(sketch, "E308", {"start": v(56.2, -40.07) * mm, "end": v(56.2, -15.43) * mm});
            skLineSegment(sketch, "E309", {"start": v(54.67, -15.43) * mm, "end": v(54.67, -40.07) * mm});
            skLineSegment(sketch, "E310", {"start": v(53.13, -40.07) * mm, "end": v(53.13, -15.43) * mm});
            skLineSegment(sketch, "E311", {"start": v(51.6, -15.43) * mm, "end": v(51.6, -40.07) * mm});
            skArc(sketch, "E312", {"start": v(53.13, -40.07) * mm, "mid": v(53.9, -40.82) * mm, "end": v(54.67, -40.07) * mm});
            skArc(sketch, "E313", {"start": v(50.07, -40.07) * mm, "mid": v(50.83, -40.82) * mm, "end": v(51.6, -40.07) * mm});
            skLineSegment(sketch, "E314", {"start": v(50.07, -40.07) * mm, "end": v(50.07, -15.43) * mm});
            skLineSegment(sketch, "E315", {"start": v(48.53, -15.43) * mm, "end": v(48.53, -40.07) * mm});
            skArc(sketch, "E316", {"start": v(47, -40.07) * mm, "mid": v(47.77, -40.82) * mm, "end": v(48.53, -40.07) * mm});
            skLineSegment(sketch, "E317", {"start": v(47, -40.07) * mm, "end": v(47, -15.43) * mm});
            skLineSegment(sketch, "E318", {"start": v(45.47, -15.43) * mm, "end": v(45.47, -40.07) * mm});
            skArc(sketch, "E319", {"start": v(43.94, -40.07) * mm, "mid": v(44.7, -40.82) * mm, "end": v(45.47, -40.07) * mm});
            skLineSegment(sketch, "E320", {"start": v(43.94, -40.07) * mm, "end": v(43.94, -16.84) * mm});
            skLineSegment(sketch, "E321", {"start": v(42.4, -16.84) * mm, "end": v(42.4, -40.07) * mm});
            skArc(sketch, "E322", {"start": v(40.87, -40.07) * mm, "mid": v(41.64, -40.82) * mm, "end": v(42.4, -40.07) * mm});
            skLineSegment(sketch, "E323", {"start": v(40.87, -40.07) * mm, "end": v(40.87, -16.84) * mm});
            skLineSegment(sketch, "E324", {"start": v(39.34, -16.84) * mm, "end": v(39.34, -40.02) * mm});
            skArc(sketch, "E325", {"start": v(37.8, -40.01) * mm, "mid": v(38.57, -40.77) * mm, "end": v(39.34, -40.01) * mm});
            skLineSegment(sketch, "E326", {"start": v(37.8, -40.01) * mm, "end": v(37.8, -15.43) * mm});
            skLineSegment(sketch, "E327", {"start": v(36.27, -15.43) * mm, "end": v(36.27, -38.74) * mm});
            skArc(sketch, "E328", {"start": v(36.04, -39.27) * mm, "mid": v(36.21, -39.03) * mm, "end": v(36.27, -38.74) * mm});
            skArc(sketch, "E329", {"start": v(59.26, -40.07) * mm, "mid": v(60.03, -40.82) * mm, "end": v(60.8, -40.07) * mm});
            skArc(sketch, "E330", {"start": v(62.33, -15.43) * mm, "mid": v(61.56, -14.67) * mm, "end": v(60.8, -15.43) * mm});
            skLineSegment(sketch, "E331.trimOffspring", {"start": v(36.27, -40) * mm, "end": v(36.27, -40.07) * mm});
            skArc(sketch, "E332", {"start": v(35.2, -39.24) * mm, "mid": v(35.62, -39.4) * mm, "end": v(36.04, -39.27) * mm});
            skArc(sketch, "E333.MirrorCS", {"start": v(33.05, 7.98) * mm, "mid": v(33.92, 5.37) * mm, "end": v(36.18, 3.81) * mm});
            skArc(sketch, "E334.MirrorCS", {"start": v(39.1, 2.36) * mm, "mid": v(37.69, 3.19) * mm, "end": v(36.18, 3.81) * mm});
            skArc(sketch, "E335.MirrorCS", {"start": v(42.11, -7.48) * mm, "mid": v(42.1, -2.1) * mm, "end": v(39.1, 2.36) * mm});
            skArc(sketch, "E336.MirrorCS", {"start": v(34.85, -5.22) * mm, "mid": v(37.28, -10.22) * mm, "end": v(42.11, -7.48) * mm});
            skLineSegment(sketch, "E337.MirrorCS", {"start": v(34.85, -5.22) * mm, "end": v(33.05, -5.22) * mm});
            skLineSegment(sketch, "E338.MirrorCS", {"start": v(33.05, -5.22) * mm, "end": v(33.08, -35.14) * mm});
            skLineSegment(sketch, "E339", {"start": v(33.05, 7.98) * mm, "end": v(33.04, 9.3) * mm});
            skArc(sketch, "E340.MirrorCS", {"start": v(80.67, 44.77) * mm, "mid": v(85.16, 42.91) * mm, "end": v(87.02, 38.42) * mm});
            skLineSegment(sketch, "E341.MirrorCS", {"start": v(83.84, 40.01) * mm, "end": v(75.92, 40.01) * mm});
            skArc(sketch, "E342.MirrorCS", {"start": v(75.71, 40.01) * mm, "mid": v(74.32, 40.82) * mm, "end": v(72.93, 40.01) * mm});
            skLineSegment(sketch, "E343.MirrorCS", {"start": v(72.75, 40.01) * mm, "end": v(64.8, 40.01) * mm});
            skLineSegment(sketch, "E344.MirrorCS", {"start": v(64.8, 40.01) * mm, "end": v(64.8, 38.42) * mm});
            skLineSegment(sketch, "E345.MirrorCS", {"start": v(68.32, 38.42) * mm, "end": v(64.8, 38.42) * mm});
            skArc(sketch, "E346.MirrorCS", {"start": v(68.43, 35.5) * mm, "mid": v(68.05, 36.95) * mm, "end": v(68.32, 38.42) * mm});
            skLineSegment(sketch, "E347.MirrorCS", {"start": v(73.89, 35.24) * mm, "end": v(73.89, 24.42) * mm});
            skLineSegment(sketch, "E348.MirrorCS", {"start": v(74.78, 35.24) * mm, "end": v(74.78, 24.42) * mm});
            skLineSegment(sketch, "E349.MirrorCS", {"start": v(73.89, 35.24) * mm, "end": v(74.78, 35.24) * mm});
            skLineSegment(sketch, "E350.MirrorCS", {"start": v(72.93, 38.42) * mm, "end": v(69.3, 38.42) * mm});
            skArc(sketch, "E351.MirrorCS", {"start": v(72.93, 38.42) * mm, "mid": v(74.32, 37.62) * mm, "end": v(75.71, 38.42) * mm});
            skLineSegment(sketch, "E352.MirrorCS", {"start": v(83.84, 38.42) * mm, "end": v(75.71, 38.42) * mm});
            skLineSegment(sketch, "E353.MirrorCS", {"start": v(83.84, 38.42) * mm, "end": v(83.84, 40.01) * mm});
            skArc(sketch, "E354.MirrorCS", {"start": v(69.94, 35.02) * mm, "mid": v(68.99, 36.6) * mm, "end": v(69.3, 38.42) * mm});
            skArc(sketch, "E355.MirrorCS", {"start": v(69.94, 35.02) * mm, "mid": v(68.61, 29.97) * mm, "end": v(68.28, 35.18) * mm});
            skArc(sketch, "E356.MirrorCS", {"start": v(68.43, 35.5) * mm, "mid": v(68.43, 35.3) * mm, "end": v(68.28, 35.18) * mm});
            skLineSegment(sketch, "E357.MirrorCS", {"start": v(87, 7.98) * mm, "end": v(87.02, 9.3) * mm});
            skArc(sketch, "E358.MirrorCS", {"start": v(87.02, 33.83) * mm, "mid": v(86.26, 34.6) * mm, "end": v(87.02, 35.36) * mm});
            skLineSegment(sketch, "E359.MirrorCS", {"start": v(87.02, 33.83) * mm, "end": v(87.02, 32.3) * mm});
            skArc(sketch, "E360.MirrorCS", {"start": v(87.02, 9.3) * mm, "mid": v(86.26, 10.07) * mm, "end": v(87.02, 10.83) * mm});
            skArc(sketch, "E361.MirrorCS", {"start": v(87.02, 27.7) * mm, "mid": v(86.26, 28.46) * mm, "end": v(87.02, 29.23) * mm});
            skLineSegment(sketch, "E362.MirrorCS", {"start": v(87.02, 36.9) * mm, "end": v(87.02, 35.36) * mm});
            skLineSegment(sketch, "E363.MirrorCS", {"start": v(87.02, 15.43) * mm, "end": v(87.02, 13.9) * mm});
            skLineSegment(sketch, "E364.MirrorCS", {"start": v(87.02, 24.63) * mm, "end": v(87.02, 23.1) * mm});
            skLineSegment(sketch, "E365.MirrorCS", {"start": v(87.02, 21.56) * mm, "end": v(87.02, 20.03) * mm});
            skLineSegment(sketch, "E366.MirrorCS", {"start": v(87.02, 18.5) * mm, "end": v(87.02, 16.96) * mm});
            skArc(sketch, "E367.MirrorCS", {"start": v(87.02, 30.76) * mm, "mid": v(86.26, 31.53) * mm, "end": v(87.02, 32.3) * mm});
            skArc(sketch, "E368.MirrorCS", {"start": v(87.02, 21.56) * mm, "mid": v(86.26, 22.33) * mm, "end": v(87.02, 23.1) * mm});
            skLineSegment(sketch, "E369.MirrorCS", {"start": v(87.02, 30.76) * mm, "end": v(87.02, 29.23) * mm});
            skArc(sketch, "E370.MirrorCS", {"start": v(87.02, 24.63) * mm, "mid": v(86.26, 25.4) * mm, "end": v(87.02, 26.16) * mm});
            skArc(sketch, "E371.MirrorCS", {"start": v(87.02, 36.9) * mm, "mid": v(86.26, 37.66) * mm, "end": v(87.02, 38.42) * mm});
            skLineSegment(sketch, "E372.MirrorCS", {"start": v(87.02, 12.37) * mm, "end": v(87.02, 10.83) * mm});
            skLineSegment(sketch, "E373.MirrorCS", {"start": v(87.02, 27.7) * mm, "end": v(87.02, 26.16) * mm});
            skArc(sketch, "E374.MirrorCS", {"start": v(87.02, 15.43) * mm, "mid": v(86.26, 16.2) * mm, "end": v(87.02, 16.96) * mm});
            skArc(sketch, "E375.MirrorCS", {"start": v(87.02, 12.37) * mm, "mid": v(86.26, 13.13) * mm, "end": v(87.02, 13.9) * mm});
            skArc(sketch, "E376.MirrorCS", {"start": v(87.02, 18.5) * mm, "mid": v(86.26, 19.26) * mm, "end": v(87.02, 20.03) * mm});
            skArc(sketch, "E377.MirrorCS", {"start": v(73.06, -40.07) * mm, "mid": v(72.3, -40.82) * mm, "end": v(71.53, -40.07) * mm});
            skArc(sketch, "E378.MirrorCS", {"start": v(79.2, -40.07) * mm, "mid": v(78.43, -40.82) * mm, "end": v(77.66, -40.07) * mm});
            skArc(sketch, "E379.MirrorCS", {"start": v(70, -40.07) * mm, "mid": v(69.23, -40.82) * mm, "end": v(68.46, -40.07) * mm});
            skArc(sketch, "E380.MirrorCS", {"start": v(63.86, -13.92) * mm, "mid": v(64.63, -13.17) * mm, "end": v(65.4, -13.92) * mm});
            skArc(sketch, "E381.MirrorCS", {"start": v(66.93, -40.07) * mm, "mid": v(66.16, -40.82) * mm, "end": v(65.4, -40.07) * mm});
            skArc(sketch, "E382.MirrorCS", {"start": v(66.93, -13.47) * mm, "mid": v(67.7, -12.71) * mm, "end": v(68.46, -13.47) * mm});
            skLineSegment(sketch, "E383.MirrorCS", {"start": v(73.58, 23.8) * mm, "end": v(73.56, 23.8) * mm});
            skArc(sketch, "E384.MirrorCS", {"start": v(60.8, -40.07) * mm, "mid": v(60.03, -40.82) * mm, "end": v(59.26, -40.07) * mm});
            skArc(sketch, "E385.MirrorCS", {"start": v(60.8, -15.43) * mm, "mid": v(61.56, -14.67) * mm, "end": v(62.33, -15.43) * mm});
            skArc(sketch, "E386.MirrorCS", {"start": v(76.13, -16.84) * mm, "mid": v(76.9, -16.09) * mm, "end": v(77.66, -16.84) * mm});
            skArc(sketch, "E387.MirrorCS", {"start": v(73.06, -15.43) * mm, "mid": v(73.83, -14.67) * mm, "end": v(74.6, -15.43) * mm});
            skArc(sketch, "E388.MirrorCS", {"start": v(73.33, 23.8) * mm, "mid": v(73.72, 24.01) * mm, "end": v(73.89, 24.42) * mm});
            skArc(sketch, "E389.MirrorCS", {"start": v(75.34, 23.8) * mm, "mid": v(74.95, 24.01) * mm, "end": v(74.78, 24.42) * mm});
            skLineSegment(sketch, "E390.MirrorCS", {"start": v(83.8, -40) * mm, "end": v(83.8, -40.07) * mm});
            skArc(sketch, "E391.MirrorCS", {"start": v(82.26, -40.01) * mm, "mid": v(81.5, -40.77) * mm, "end": v(80.72, -40.01) * mm});
            skLineSegment(sketch, "E392.MirrorCS", {"start": v(72.93, 40.01) * mm, "end": v(72.75, 40.01) * mm});
            skArc(sketch, "E393.MirrorCS", {"start": v(70, -13.92) * mm, "mid": v(70.76, -13.17) * mm, "end": v(71.53, -13.92) * mm});
            skArc(sketch, "E394.MirrorCS", {"start": v(63.86, -40.07) * mm, "mid": v(63.1, -40.82) * mm, "end": v(62.33, -40.07) * mm});
            skLineSegment(sketch, "E395.MirrorCS", {"start": v(75.92, 40.01) * mm, "end": v(75.71, 40.01) * mm});
            skArc(sketch, "E396.MirrorCS", {"start": v(76.13, -40.07) * mm, "mid": v(75.36, -40.82) * mm, "end": v(74.6, -40.07) * mm});
            skArc(sketch, "E397.MirrorCS", {"start": v(84.86, -39.24) * mm, "mid": v(84.45, -39.4) * mm, "end": v(84.02, -39.27) * mm});
            skLineSegment(sketch, "E398.MirrorCS", {"start": v(85.21, -5.22) * mm, "end": v(87, -5.22) * mm});
            skArc(sketch, "E399.MirrorCS", {"start": v(79.2, -16.84) * mm, "mid": v(79.96, -16.09) * mm, "end": v(80.72, -16.84) * mm});
            skArc(sketch, "E400.MirrorCS", {"start": v(86.98, -35.14) * mm, "mid": v(86.3, -37.4) * mm, "end": v(84.86, -39.24) * mm});
            skLineSegment(sketch, "E401.MirrorCS", {"start": v(56.86, 10.95) * mm, "end": v(56.06, 10.5) * mm});
            skArc(sketch, "E402.MirrorCS", {"start": v(84.02, -39.27) * mm, "mid": v(83.85, -39.03) * mm, "end": v(83.8, -38.74) * mm});
            skLineSegment(sketch, "E403.MirrorCS", {"start": v(56.06, 10.5) * mm, "end": v(56.06, 5.9) * mm});
            skLineSegment(sketch, "E404.MirrorCS", {"start": v(56.86, 14.61) * mm, "end": v(56.86, 10.95) * mm});
            skArc(sketch, "E405.MirrorCS", {"start": v(82.26, -15.43) * mm, "mid": v(83.02, -14.67) * mm, "end": v(83.8, -15.43) * mm});
            skLineSegment(sketch, "E406.MirrorCS", {"start": v(56.06, 5.9) * mm, "end": v(55.27, 5.45) * mm});
            skLineSegment(sketch, "E407.MirrorCS", {"start": v(73.56, 27.58) * mm, "end": v(73.56, 27.57) * mm});
            skLineSegment(sketch, "E408.MirrorCS", {"start": v(75.1, 27.58) * mm, "end": v(75.1, 27.57) * mm});
            skArc(sketch, "E409.MirrorCS", {"start": v(80.97, 2.36) * mm, "mid": v(82.37, 3.19) * mm, "end": v(83.88, 3.81) * mm});
            skLineSegment(sketch, "E410.MirrorCS", {"start": v(55.27, -0.05) * mm, "end": v(53.68, -0.97) * mm});
            skLineSegment(sketch, "E411.MirrorCS", {"start": v(60.03, 16.45) * mm, "end": v(56.86, 14.61) * mm});
            skLineSegment(sketch, "E412.MirrorCS", {"start": v(53.68, -8.3) * mm, "end": v(60.03, -11.96) * mm});
            skLineSegment(sketch, "E413.MirrorCS", {"start": v(77.66, -16.84) * mm, "end": v(77.66, -40.07) * mm});
            skLineSegment(sketch, "E414.MirrorCS", {"start": v(53.68, -0.97) * mm, "end": v(53.68, -8.3) * mm});
            skLineSegment(sketch, "E415.MirrorCS", {"start": v(71.53, -13.92) * mm, "end": v(71.53, -40.07) * mm});
            skLineSegment(sketch, "E416.MirrorCS", {"start": v(82.26, -40.01) * mm, "end": v(82.26, -15.43) * mm});
            skLineSegment(sketch, "E417.MirrorCS", {"start": v(87, -5.22) * mm, "end": v(86.98, -35.14) * mm});
            skArc(sketch, "E418.MirrorCS", {"start": v(77.95, -7.48) * mm, "mid": v(77.97, -2.1) * mm, "end": v(80.97, 2.36) * mm});
            skLineSegment(sketch, "E419.MirrorCS", {"start": v(83.8, -15.43) * mm, "end": v(83.8, -38.74) * mm});
            skPoint(sketch, "E420.MirrorP", {"position": v(74.33, 35.24) * mm});
            skArc(sketch, "E421.MirrorCS", {"start": v(85.21, -5.22) * mm, "mid": v(82.78, -10.22) * mm, "end": v(77.95, -7.48) * mm});
            skLineSegment(sketch, "E422.MirrorCS", {"start": v(60.8, -40.07) * mm, "end": v(60.8, -15.43) * mm});
            skPoint(sketch, "E423.MirrorP", {"position": v(56.86, -10.13) * mm});
            skLineSegment(sketch, "E424.MirrorCS", {"start": v(76.13, -40.07) * mm, "end": v(76.13, -16.84) * mm});
            skPoint(sketch, "E425.MirrorP", {"position": v(87.02, -34.47) * mm});
            skPoint(sketch, "E426.MirrorP", {"position": v(69.94, 35.02) * mm});
            skLineSegment(sketch, "E427.MirrorCS", {"start": v(63.86, -40.07) * mm, "end": v(63.86, -13.92) * mm});
            skLineSegment(sketch, "E428.MirrorCS", {"start": v(74.6, -15.43) * mm, "end": v(74.6, -40.07) * mm});
            skArc(sketch, "E429.MirrorCS", {"start": v(75.34, 23.8) * mm, "mid": v(74.32, 11.04) * mm, "end": v(73.35, 23.8) * mm});
            skPoint(sketch, "E430.MirrorP", {"position": v(69.97, 35) * mm});
            skArc(sketch, "E431.MirrorCS", {"start": v(87, 7.98) * mm, "mid": v(86.14, 5.37) * mm, "end": v(83.88, 3.81) * mm});
            skLineSegment(sketch, "E432.MirrorCS", {"start": v(65.4, -13.92) * mm, "end": v(65.4, -40.07) * mm});
            skLineSegment(sketch, "E433.MirrorCS", {"start": v(55.27, 5.45) * mm, "end": v(55.27, -0.05) * mm});
            skLineSegment(sketch, "E434.MirrorCS", {"start": v(73.06, -40.07) * mm, "end": v(73.06, -15.43) * mm});
            skPoint(sketch, "E435.MirrorP", {"position": v(85.73, -41.44) * mm});
            skLineSegment(sketch, "E436.MirrorCS", {"start": v(79.2, -40.07) * mm, "end": v(79.2, -16.84) * mm});
            skLineSegment(sketch, "E437.MirrorCS", {"start": v(70, -40.07) * mm, "end": v(70, -13.92) * mm});
            skLineSegment(sketch, "E438.MirrorCS", {"start": v(68.46, -13.47) * mm, "end": v(68.46, -40.07) * mm});
            skLineSegment(sketch, "E439.MirrorCS", {"start": v(62.33, -15.43) * mm, "end": v(62.33, -40.07) * mm});
            skLineSegment(sketch, "E440.MirrorCS", {"start": v(66.93, -40.07) * mm, "end": v(66.93, -13.47) * mm});
            skLineSegment(sketch, "E441", {"start": v(39.4, 44.77) * mm, "end": v(80.67, 44.77) * mm});
            skArc(sketch, "E442", {"start": v(64.34, 20.82) * mm, "mid": v(60.03, 22.07) * mm, "end": v(55.77, 20.7) * mm});
            skArc(sketch, "E443", {"start": v(61.62, 27.05) * mm, "mid": v(61.37, 26.49) * mm, "end": v(61.25, 25.88) * mm});
            skArc(sketch, "E444", {"start": v(61.35, 24.9) * mm, "mid": v(61.71, 24.22) * mm, "end": v(62.42, 23.9) * mm});
            skArc(sketch, "E445", {"start": v(62.41, 28.44) * mm, "mid": v(62.06, 28.4) * mm, "end": v(61.72, 28.32) * mm});
            skArc(sketch, "E446", {"start": v(61.72, 28.32) * mm, "mid": v(61.3, 28.15) * mm, "end": v(60.91, 27.9) * mm});
            skArc(sketch, "E447", {"start": v(60.91, 27.9) * mm, "mid": v(60.55, 27.5) * mm, "end": v(60.3, 27.03) * mm});
            skArc(sketch, "E448", {"start": v(60.3, 27.03) * mm, "mid": v(60.14, 26.47) * mm, "end": v(60.09, 25.88) * mm});
            skArc(sketch, "E449", {"start": v(60.09, 25.88) * mm, "mid": v(60.08, 25.88) * mm, "end": v(60.08, 25.88) * mm});
            skArc(sketch, "E450", {"start": v(60.12, 25.07) * mm, "mid": v(60.2, 24.69) * mm, "end": v(60.31, 24.32) * mm});
            skArc(sketch, "E451", {"start": v(60.31, 24.32) * mm, "mid": v(60.45, 24.03) * mm, "end": v(60.64, 23.76) * mm});
            skArc(sketch, "E452", {"start": v(60.64, 23.76) * mm, "mid": v(60.9, 23.5) * mm, "end": v(61.2, 23.28) * mm});
            skArc(sketch, "E453", {"start": v(61.2, 23.28) * mm, "mid": v(61.54, 23.12) * mm, "end": v(61.9, 23.02) * mm});
            skArc(sketch, "E454", {"start": v(61.9, 23.02) * mm, "mid": v(62.14, 22.97) * mm, "end": v(62.38, 22.95) * mm});
            skArc(sketch, "E455", {"start": v(62.38, 22.95) * mm, "mid": v(62.4, 22.95) * mm, "end": v(62.42, 22.95) * mm});
            skLineSegment(sketch, "E456", {"start": v(62.6, 27.5) * mm, "end": v(62.6, 27.5) * mm});
            skLineSegment(sketch, "E457", {"start": v(62.62, 23.88) * mm, "end": v(62.62, 23.87) * mm});
            skLineSegment(sketch, "E458.trimOffspring", {"start": v(62.42, 27.47) * mm, "end": v(62.41, 28.44) * mm});
            skLineSegment(sketch, "E459", {"start": v(62.42, 23.42) * mm, "end": v(62.42, 22.95) * mm});
            skArc(sketch, "E460.trimOffspring", {"start": v(62.62, 22.94) * mm, "mid": v(62.62, 22.94) * mm, "end": v(62.63, 22.94) * mm});
            skLineSegment(sketch, "E461.trimOffspring", {"start": v(62.42, 23.9) * mm, "end": v(62.42, 23.42) * mm});
            skArc(sketch, "E462.trimOffspring", {"start": v(62.42, 27.47) * mm, "mid": v(61.98, 27.33) * mm, "end": v(61.62, 27.05) * mm});
            skPoint(sketch, "E463.orphan", {"position": v(61.24, 25.62) * mm});
            skArc(sketch, "E464.MirrorCS", {"start": v(62.8, 27.48) * mm, "mid": v(63.23, 27.34) * mm, "end": v(63.6, 27.06) * mm});
            skArc(sketch, "E465.MirrorCS", {"start": v(63.6, 27.06) * mm, "mid": v(63.85, 26.5) * mm, "end": v(63.98, 25.9) * mm});
            skArc(sketch, "E466.MirrorCS", {"start": v(63.9, 24.92) * mm, "mid": v(63.53, 24.23) * mm, "end": v(62.83, 23.9) * mm});
            skArc(sketch, "E467.MirrorCS", {"start": v(62.88, 22.95) * mm, "mid": v(62.86, 22.95) * mm, "end": v(62.84, 22.95) * mm});
            skArc(sketch, "E468.MirrorCS", {"start": v(63.35, 23.02) * mm, "mid": v(63.12, 22.98) * mm, "end": v(62.88, 22.95) * mm});
            skArc(sketch, "E469.MirrorCS", {"start": v(64.06, 23.3) * mm, "mid": v(63.72, 23.13) * mm, "end": v(63.35, 23.02) * mm});
            skArc(sketch, "E470.MirrorCS", {"start": v(64.61, 23.78) * mm, "mid": v(64.36, 23.52) * mm, "end": v(64.06, 23.3) * mm});
            skArc(sketch, "E471.MirrorCS", {"start": v(64.93, 24.34) * mm, "mid": v(64.8, 24.05) * mm, "end": v(64.61, 23.78) * mm});
            skArc(sketch, "E472.MirrorCS", {"start": v(65.12, 25.1) * mm, "mid": v(65.05, 24.71) * mm, "end": v(64.93, 24.34) * mm});
            skArc(sketch, "E473.MirrorCS", {"start": v(65.14, 25.9) * mm, "mid": v(65.14, 25.9) * mm, "end": v(65.14, 25.9) * mm});
            skArc(sketch, "E474.MirrorCS", {"start": v(64.91, 27.05) * mm, "mid": v(65.08, 26.5) * mm, "end": v(65.14, 25.9) * mm});
            skArc(sketch, "E475.MirrorCS", {"start": v(64.3, 27.9) * mm, "mid": v(64.66, 27.52) * mm, "end": v(64.91, 27.05) * mm});
            skArc(sketch, "E476.MirrorCS", {"start": v(63.48, 28.33) * mm, "mid": v(63.91, 28.16) * mm, "end": v(64.3, 27.9) * mm});
            skArc(sketch, "E477.MirrorCS", {"start": v(62.8, 28.44) * mm, "mid": v(63.14, 28.4) * mm, "end": v(63.48, 28.33) * mm});
            skLineSegment(sketch, "E478.MirrorCS", {"start": v(62.8, 27.48) * mm, "end": v(62.8, 28.44) * mm});
            skLineSegment(sketch, "E479.MirrorCS", {"start": v(62.83, 23.9) * mm, "end": v(62.83, 23.42) * mm});
            skLineSegment(sketch, "E480.MirrorCS", {"start": v(62.83, 23.42) * mm, "end": v(62.84, 22.95) * mm});
            skArc(sketch, "E481", {"start": v(62.62, 23.87) * mm, "mid": v(62.62, 23.87) * mm, "end": v(62.62, 23.87) * mm});
            skLineSegment(sketch, "E482.0", {"start": v(60.08, 25.5) * mm, "end": v(61.25, 25.5) * mm});
            skLineSegment(sketch, "E483.0", {"start": v(60.08, 25.88) * mm, "end": v(61.25, 25.88) * mm});
            skLineSegment(sketch, "E484.trimOffspring", {"start": v(63.98, 25.9) * mm, "end": v(65.15, 25.9) * mm});
            skPoint(sketch, "E485.orphan", {"position": v(62.62, 25.7) * mm});
            skLineSegment(sketch, "E486.trimOffspring", {"start": v(63.98, 25.52) * mm, "end": v(65.15, 25.53) * mm});
            skPoint(sketch, "E487.MirrorCS.end.orphan", {"position": v(62.63, 23.87) * mm});
            skPoint(sketch, "E487.MirrorCS.start.orphan", {"position": v(62.83, 23.9) * mm});
            skPoint(sketch, "E488.MirrorCS.end.orphan", {"position": v(63, 22.94) * mm});
            skPoint(sketch, "E488.MirrorCS.start.orphan", {"position": v(63.22, 22.95) * mm});
            skPoint(sketch, "E489.orphan", {"position": v(62.6, 28.44) * mm});
            skPoint(sketch, "E490.MirrorCS.end.orphan", {"position": v(62.8, 27.48) * mm});
            skArc(sketch, "E491.trimOffspring", {"start": v(60.08, 25.5) * mm, "mid": v(60.1, 25.29) * mm, "end": v(60.12, 25.07) * mm});
            skArc(sketch, "E492.trimOffspring", {"start": v(61.25, 25.5) * mm, "mid": v(61.28, 25.2) * mm, "end": v(61.35, 24.9) * mm});
            skArc(sketch, "E493.trimOffspring", {"start": v(63.98, 25.52) * mm, "mid": v(63.95, 25.22) * mm, "end": v(63.9, 24.92) * mm});
            skArc(sketch, "E494.trimOffspring", {"start": v(65.15, 25.53) * mm, "mid": v(65.14, 25.31) * mm, "end": v(65.12, 25.1) * mm});
            skText(sketch, "E495", { "text": "X", "fontName": "OpenSans-Bold.ttf"});
            skLineSegment(sketch, "E496", {"start": v(64.34, 19.56) * mm, "end": v(64.34, 20.82) * mm});
            skLineSegment(sketch, "E497", {"start": v(64.34, 20.82) * mm, "end": v(64.34, 19.56) * mm});
            skCircle(sketch, "E498", {"center": v(62.62, 25.7) * mm, "radius": 0.65 * mm});
            skArc(sketch, "E499.0", {"start": v(64.34, 19.56) * mm, "mid": v(60.02, 21.05) * mm, "end": v(55.77, 19.4) * mm});
            skLineSegment(sketch, "E500", {"start": v(55.77, 20.7) * mm, "end": v(55.77, 19.4) * mm});
            skLineSegment(sketch, "E501.trimOffspring", {"start": v(80.72, -16.84) * mm, "end": v(80.72, -40.02) * mm});
            skArc(sketch, "E502.MirrorCS", {"start": v(40.87, -16.84) * mm, "mid": v(40.1, -16.09) * mm, "end": v(39.34, -16.84) * mm});
            skArc(sketch, "E503.MirrorCS", {"start": v(37.8, -15.43) * mm, "mid": v(37.04, -14.67) * mm, "end": v(36.27, -15.43) * mm});
            skArc(sketch, "E504.MirrorCS", {"start": v(43.94, -16.84) * mm, "mid": v(43.17, -16.09) * mm, "end": v(42.4, -16.84) * mm});
            skArc(sketch, "E505.MirrorCS", {"start": v(47, -15.43) * mm, "mid": v(46.24, -14.67) * mm, "end": v(45.47, -15.43) * mm});
            skArc(sketch, "E506.MirrorCS", {"start": v(50.07, -13.92) * mm, "mid": v(49.3, -13.17) * mm, "end": v(48.53, -13.92) * mm});
            skArc(sketch, "E507.MirrorCS", {"start": v(56.2, -13.92) * mm, "mid": v(55.43, -13.17) * mm, "end": v(54.67, -13.92) * mm});
            skArc(sketch, "E508.MirrorCS", {"start": v(53.13, -13.47) * mm, "mid": v(52.37, -12.71) * mm, "end": v(51.6, -13.47) * mm});
            skLineSegment(sketch, "E509.MirrorCS", {"start": v(56.2, -40.07) * mm, "end": v(56.2, -13.92) * mm});
            skLineSegment(sketch, "E510.MirrorCS", {"start": v(54.67, -13.92) * mm, "end": v(54.67, -40.07) * mm});
            skLineSegment(sketch, "E511.MirrorCS", {"start": v(53.13, -40.07) * mm, "end": v(53.13, -13.47) * mm});
            skLineSegment(sketch, "E512.MirrorCS", {"start": v(51.6, -13.47) * mm, "end": v(51.6, -40.07) * mm});
            skLineSegment(sketch, "E513.MirrorCS", {"start": v(50.07, -40.07) * mm, "end": v(50.07, -13.92) * mm});
            skLineSegment(sketch, "E514.MirrorCS", {"start": v(48.53, -13.92) * mm, "end": v(48.53, -40.07) * mm});
            skPoint(sketch, "E515.orphan", {"position": v(39.34, -15.43) * mm});
            skPoint(sketch, "E516.orphan", {"position": v(43.94, -15.43) * mm});
            skLineSegment(sketch, "E517.trimOffspring", {"start": v(60.03, -40.06) * mm, "end": v(60.03, -40.82) * mm});
            skArc(sketch, "E518.MirrorCS", {"start": v(3.83, -15.43) * mm, "mid": v(4.6, -14.67) * mm, "end": v(5.37, -15.43) * mm});
            skArc(sketch, "E519.MirrorCS", {"start": v(9.96, -15.43) * mm, "mid": v(10.73, -14.67) * mm, "end": v(11.5, -15.43) * mm});
            skArc(sketch, "E520.MirrorCS", {"start": v(22.23, -15.43) * mm, "mid": v(23, -14.67) * mm, "end": v(23.76, -15.43) * mm});
            skArc(sketch, "E521.MirrorCS", {"start": v(19.16, -15.43) * mm, "mid": v(19.93, -14.67) * mm, "end": v(20.7, -15.43) * mm});
            skArc(sketch, "E522.MirrorCS", {"start": v(16.1, -15.43) * mm, "mid": v(16.86, -14.67) * mm, "end": v(17.63, -15.43) * mm});
            skArc(sketch, "E523.MirrorCS", {"start": v(13.03, -15.43) * mm, "mid": v(13.8, -14.67) * mm, "end": v(14.56, -15.43) * mm});
            skArc(sketch, "E524.MirrorCS", {"start": v(6.9, -15.43) * mm, "mid": v(7.66, -14.67) * mm, "end": v(8.43, -15.43) * mm});
            skLineSegment(sketch, "E525.MirrorCS", {"start": v(20.7, -15.43) * mm, "end": v(20.7, -40.02) * mm});
            skLineSegment(sketch, "E526.MirrorCS", {"start": v(19.16, -40.07) * mm, "end": v(19.16, -15.43) * mm});
            skLineSegment(sketch, "E527.MirrorCS", {"start": v(17.63, -15.43) * mm, "end": v(17.63, -40.07) * mm});
            skLineSegment(sketch, "E528.MirrorCS", {"start": v(16.1, -40.07) * mm, "end": v(16.1, -15.43) * mm});
            skLineSegment(sketch, "E529.0", {"start": v(-53.88, -7.68) * mm, "end": v(-60.23, -11.34) * mm});
            skLineSegment(sketch, "E529.4", {"start": v(-55.46, 0.57) * mm, "end": v(-53.88, -0.35) * mm});
            skLineSegment(sketch, "E529.5", {"start": v(-53.88, -0.35) * mm, "end": v(-53.88, -7.68) * mm});
            skPoint(sketch, "E529.0.midPoint", {"position": v(-57.05, -9.51) * mm});
            skLineSegment(sketch, "E530.4", {"start": v(-56.26, 6.53) * mm, "end": v(-55.46, 6.07) * mm});
            skLineSegment(sketch, "E530.5", {"start": v(-55.46, 6.07) * mm, "end": v(-55.46, 0.57) * mm});
            skLineSegment(sketch, "E531.4", {"start": v(-57.05, 11.57) * mm, "end": v(-56.26, 11.11) * mm});
            skLineSegment(sketch, "E531.5", {"start": v(-56.26, 11.11) * mm, "end": v(-56.26, 6.53) * mm});
            skLineSegment(sketch, "E532.4", {"start": v(-60.23, 17.07) * mm, "end": v(-57.05, 15.23) * mm});
            skLineSegment(sketch, "E532.5", {"start": v(-57.05, 15.23) * mm, "end": v(-57.05, 11.57) * mm});
            skLineSegment(sketch, "E533.left", {"start": v(-87.21, 37.51) * mm, "end": v(-87.21, 35.98) * mm});
            skArc(sketch, "E534.filletArc", {"start": v(-80.86, 45.4) * mm, "mid": v(-85.35, 43.53) * mm, "end": v(-87.21, 39.04) * mm});
            skArc(sketch, "E535.filletArc", {"start": v(-87.18, -34.52) * mm, "mid": v(-86.5, -36.77) * mm, "end": v(-85.06, -38.62) * mm});
            skLineSegment(sketch, "E536", {"start": v(-84.04, 39.04) * mm, "end": v(-84.04, 40.63) * mm});
            skLineSegment(sketch, "E537", {"start": v(-84.04, 40.63) * mm, "end": v(-76.11, 40.63) * mm});
            skLineSegment(sketch, "E538", {"start": v(-64.99, 40.63) * mm, "end": v(-64.99, 39.04) * mm});
            skLineSegment(sketch, "E539", {"start": v(-84.04, 39.04) * mm, "end": v(-75.9, 39.04) * mm});
            skLineSegment(sketch, "E540.MirrorCS", {"start": v(-73.76, 28.2) * mm, "end": v(-73.76, 28.2) * mm});
            skLineSegment(sketch, "E541.MirrorCS", {"start": v(-75.29, 28.2) * mm, "end": v(-75.29, 28.19) * mm});
            skLineSegment(sketch, "E542.MirrorCS", {"start": v(-74.08, 35.86) * mm, "end": v(-74.97, 35.86) * mm});
            skLineSegment(sketch, "E543", {"start": v(-73.77, 24.43) * mm, "end": v(-73.76, 24.43) * mm});
            skLineSegment(sketch, "E544.0", {"start": v(-74.97, 35.86) * mm, "end": v(-74.97, 25.04) * mm});
            skLineSegment(sketch, "E545.0", {"start": v(-74.08, 35.86) * mm, "end": v(-74.08, 25.04) * mm});
            skArc(sketch, "E546", {"start": v(-75.53, 24.42) * mm, "mid": v(-74.51, 11.66) * mm, "end": v(-73.55, 24.42) * mm});
            skArc(sketch, "E547", {"start": v(-87.21, 9.92) * mm, "mid": v(-86.46, 10.69) * mm, "end": v(-87.21, 11.45) * mm});
            skArc(sketch, "E548", {"start": v(-87.21, 12.99) * mm, "mid": v(-86.46, 13.75) * mm, "end": v(-87.21, 14.52) * mm});
            skArc(sketch, "E549", {"start": v(-87.21, 16.05) * mm, "mid": v(-86.46, 16.82) * mm, "end": v(-87.21, 17.58) * mm});
            skArc(sketch, "E550", {"start": v(-87.21, 19.12) * mm, "mid": v(-86.46, 19.88) * mm, "end": v(-87.21, 20.65) * mm});
            skArc(sketch, "E551", {"start": v(-87.21, 22.18) * mm, "mid": v(-86.46, 22.95) * mm, "end": v(-87.21, 23.71) * mm});
            skArc(sketch, "E552", {"start": v(-87.21, 25.25) * mm, "mid": v(-86.46, 26.01) * mm, "end": v(-87.21, 26.78) * mm});
            skArc(sketch, "E553", {"start": v(-87.21, 28.31) * mm, "mid": v(-86.46, 29.08) * mm, "end": v(-87.21, 29.85) * mm});
            skArc(sketch, "E554", {"start": v(-87.21, 31.38) * mm, "mid": v(-86.46, 32.15) * mm, "end": v(-87.21, 32.91) * mm});
            skArc(sketch, "E555", {"start": v(-87.21, 34.44) * mm, "mid": v(-86.46, 35.21) * mm, "end": v(-87.21, 35.98) * mm});
            skArc(sketch, "E556", {"start": v(-87.21, 37.51) * mm, "mid": v(-86.46, 38.28) * mm, "end": v(-87.21, 39.04) * mm});
            skLineSegment(sketch, "E557.trimOffspring", {"start": v(-87.21, 12.99) * mm, "end": v(-87.21, 11.45) * mm});
            skLineSegment(sketch, "E558.trimOffspring", {"start": v(-87.21, 16.05) * mm, "end": v(-87.21, 14.52) * mm});
            skLineSegment(sketch, "E559.trimOffspring", {"start": v(-87.21, 19.12) * mm, "end": v(-87.21, 17.58) * mm});
            skLineSegment(sketch, "E560.trimOffspring", {"start": v(-87.21, 22.18) * mm, "end": v(-87.21, 20.65) * mm});
            skLineSegment(sketch, "E561.trimOffspring", {"start": v(-87.21, 25.25) * mm, "end": v(-87.21, 23.71) * mm});
            skLineSegment(sketch, "E562.trimOffspring", {"start": v(-87.21, 28.31) * mm, "end": v(-87.21, 26.78) * mm});
            skLineSegment(sketch, "E563.trimOffspring", {"start": v(-87.21, 31.38) * mm, "end": v(-87.21, 29.85) * mm});
            skLineSegment(sketch, "E564.trimOffspring", {"start": v(-87.21, 34.44) * mm, "end": v(-87.21, 32.91) * mm});
            skPoint(sketch, "E565.orphan", {"position": v(-74.53, 35.86) * mm});
            skLineSegment(sketch, "E566.trimOffspring", {"start": v(-72.94, 40.63) * mm, "end": v(-64.99, 40.63) * mm});
            skLineSegment(sketch, "E567", {"start": v(-76.11, 40.63) * mm, "end": v(-75.9, 40.63) * mm});
            skArc(sketch, "E568.MirrorCS", {"start": v(-75.9, 40.63) * mm, "mid": v(-74.52, 41.44) * mm, "end": v(-73.13, 40.63) * mm});
            skArc(sketch, "E569.MirrorCS", {"start": v(-73.13, 39.04) * mm, "mid": v(-74.52, 38.24) * mm, "end": v(-75.9, 39.04) * mm});
            skLineSegment(sketch, "E570.trimOffspring", {"start": v(-73.13, 39.04) * mm, "end": v(-69.5, 39.04) * mm});
            skLineSegment(sketch, "E571.trimOffspring", {"start": v(-73.13, 40.63) * mm, "end": v(-72.94, 40.63) * mm});
            skLineSegment(sketch, "E572.trimOffspring", {"start": v(-68.51, 39.04) * mm, "end": v(-64.99, 39.04) * mm});
            skArc(sketch, "E573", {"start": v(-70.13, 35.64) * mm, "mid": v(-69.18, 37.22) * mm, "end": v(-69.5, 39.04) * mm});
            skArc(sketch, "E574.0", {"start": v(-68.62, 36.12) * mm, "mid": v(-68.25, 37.57) * mm, "end": v(-68.51, 39.04) * mm});
            skPoint(sketch, "E575.start.orphan", {"position": v(-70.13, 35.64) * mm});
            skArc(sketch, "E576.MirrorCS", {"start": v(-70.13, 35.64) * mm, "mid": v(-68.8, 30.6) * mm, "end": v(-68.47, 35.8) * mm});
            skPoint(sketch, "E577.orphan", {"position": v(-70.16, 35.61) * mm});
            skArc(sketch, "E578", {"start": v(-75.53, 24.42) * mm, "mid": v(-75.14, 24.63) * mm, "end": v(-74.97, 25.04) * mm});
            skArc(sketch, "E579.MirrorCS", {"start": v(-73.52, 24.42) * mm, "mid": v(-73.91, 24.63) * mm, "end": v(-74.08, 25.04) * mm});
            skArc(sketch, "E580", {"start": v(-68.62, 36.12) * mm, "mid": v(-68.62, 35.92) * mm, "end": v(-68.47, 35.8) * mm});
            skArc(sketch, "E581", {"start": v(-61, -39.45) * mm, "mid": v(-60.23, -40.2) * mm, "end": v(-59.46, -39.45) * mm});
            skArc(sketch, "E582", {"start": v(-57.93, -14.8) * mm, "mid": v(-58.7, -14.05) * mm, "end": v(-59.46, -14.8) * mm});
            skArc(sketch, "E583.MirrorCS", {"start": v(-87.2, 8.6) * mm, "mid": v(-86.33, 6) * mm, "end": v(-84.07, 4.43) * mm});
            skArc(sketch, "E584.MirrorCS", {"start": v(-81.16, 2.98) * mm, "mid": v(-82.57, 3.8) * mm, "end": v(-84.07, 4.43) * mm});
            skArc(sketch, "E585.MirrorCS", {"start": v(-78.14, -6.86) * mm, "mid": v(-78.16, -1.48) * mm, "end": v(-81.16, 2.98) * mm});
            skArc(sketch, "E586.MirrorCS", {"start": v(-85.4, -4.6) * mm, "mid": v(-82.97, -9.6) * mm, "end": v(-78.14, -6.86) * mm});
            skLineSegment(sketch, "E587.MirrorCS", {"start": v(-85.4, -4.6) * mm, "end": v(-87.2, -4.6) * mm});
            skLineSegment(sketch, "E588.MirrorCS", {"start": v(-87.2, -4.6) * mm, "end": v(-87.18, -34.52) * mm});
            skLineSegment(sketch, "E589", {"start": v(-87.2, 8.6) * mm, "end": v(-87.21, 9.92) * mm});
            skArc(sketch, "E590.MirrorCS", {"start": v(-39.59, 45.4) * mm, "mid": v(-35.1, 43.53) * mm, "end": v(-33.24, 39.04) * mm});
            skLineSegment(sketch, "E591.MirrorCS", {"start": v(-36.41, 40.63) * mm, "end": v(-44.34, 40.63) * mm});
            skArc(sketch, "E592.MirrorCS", {"start": v(-44.55, 40.63) * mm, "mid": v(-45.94, 41.44) * mm, "end": v(-47.32, 40.63) * mm});
            skLineSegment(sketch, "E593.MirrorCS", {"start": v(-47.51, 40.63) * mm, "end": v(-55.46, 40.63) * mm});
            skLineSegment(sketch, "E594.MirrorCS", {"start": v(-55.46, 40.63) * mm, "end": v(-55.46, 39.04) * mm});
            skLineSegment(sketch, "E595.MirrorCS", {"start": v(-51.94, 39.04) * mm, "end": v(-55.46, 39.04) * mm});
            skArc(sketch, "E596.MirrorCS", {"start": v(-51.83, 36.12) * mm, "mid": v(-52.2, 37.57) * mm, "end": v(-51.94, 39.04) * mm});
            skLineSegment(sketch, "E597.MirrorCS", {"start": v(-46.37, 35.86) * mm, "end": v(-46.37, 25.04) * mm});
            skLineSegment(sketch, "E598.MirrorCS", {"start": v(-45.48, 35.86) * mm, "end": v(-45.48, 25.04) * mm});
            skLineSegment(sketch, "E599.MirrorCS", {"start": v(-46.37, 35.86) * mm, "end": v(-45.48, 35.86) * mm});
            skLineSegment(sketch, "E600.MirrorCS", {"start": v(-47.32, 39.04) * mm, "end": v(-50.95, 39.04) * mm});
            skArc(sketch, "E601.MirrorCS", {"start": v(-47.32, 39.04) * mm, "mid": v(-45.94, 38.24) * mm, "end": v(-44.55, 39.04) * mm});
            skLineSegment(sketch, "E602.MirrorCS", {"start": v(-36.41, 39.04) * mm, "end": v(-44.55, 39.04) * mm});
            skLineSegment(sketch, "E603.MirrorCS", {"start": v(-36.41, 39.04) * mm, "end": v(-36.41, 40.63) * mm});
            skArc(sketch, "E604.MirrorCS", {"start": v(-50.32, 35.64) * mm, "mid": v(-51.27, 37.22) * mm, "end": v(-50.95, 39.04) * mm});
            skArc(sketch, "E605.MirrorCS", {"start": v(-50.32, 35.64) * mm, "mid": v(-51.65, 30.6) * mm, "end": v(-51.98, 35.8) * mm});
            skArc(sketch, "E606.MirrorCS", {"start": v(-51.83, 36.12) * mm, "mid": v(-51.83, 35.92) * mm, "end": v(-51.98, 35.8) * mm});
            skLineSegment(sketch, "E607.MirrorCS", {"start": v(-33.25, 8.6) * mm, "end": v(-33.24, 9.92) * mm});
            skArc(sketch, "E608.MirrorCS", {"start": v(-33.24, 34.44) * mm, "mid": v(-34, 35.21) * mm, "end": v(-33.24, 35.98) * mm});
            skLineSegment(sketch, "E609.MirrorCS", {"start": v(-33.24, 34.44) * mm, "end": v(-33.24, 32.91) * mm});
            skArc(sketch, "E610.MirrorCS", {"start": v(-33.24, 9.92) * mm, "mid": v(-34, 10.69) * mm, "end": v(-33.24, 11.45) * mm});
            skArc(sketch, "E611.MirrorCS", {"start": v(-33.24, 28.31) * mm, "mid": v(-34, 29.08) * mm, "end": v(-33.24, 29.85) * mm});
            skLineSegment(sketch, "E612.MirrorCS", {"start": v(-33.24, 37.51) * mm, "end": v(-33.24, 35.98) * mm});
            skLineSegment(sketch, "E613.MirrorCS", {"start": v(-33.24, 16.05) * mm, "end": v(-33.24, 14.52) * mm});
            skLineSegment(sketch, "E614.MirrorCS", {"start": v(-33.24, 25.25) * mm, "end": v(-33.24, 23.71) * mm});
            skLineSegment(sketch, "E615.MirrorCS", {"start": v(-33.24, 22.18) * mm, "end": v(-33.24, 20.65) * mm});
            skLineSegment(sketch, "E616.MirrorCS", {"start": v(-33.24, 19.12) * mm, "end": v(-33.24, 17.58) * mm});
            skArc(sketch, "E617.MirrorCS", {"start": v(-33.24, 31.38) * mm, "mid": v(-34, 32.15) * mm, "end": v(-33.24, 32.91) * mm});
            skArc(sketch, "E618.MirrorCS", {"start": v(-33.24, 22.18) * mm, "mid": v(-34, 22.95) * mm, "end": v(-33.24, 23.71) * mm});
            skLineSegment(sketch, "E619.MirrorCS", {"start": v(-33.24, 31.38) * mm, "end": v(-33.24, 29.85) * mm});
            skArc(sketch, "E620.MirrorCS", {"start": v(-33.24, 25.25) * mm, "mid": v(-34, 26.01) * mm, "end": v(-33.24, 26.78) * mm});
            skArc(sketch, "E621.MirrorCS", {"start": v(-33.24, 37.51) * mm, "mid": v(-34, 38.28) * mm, "end": v(-33.24, 39.04) * mm});
            skLineSegment(sketch, "E622.MirrorCS", {"start": v(-33.24, 12.99) * mm, "end": v(-33.24, 11.45) * mm});
            skLineSegment(sketch, "E623.MirrorCS", {"start": v(-33.24, 28.31) * mm, "end": v(-33.24, 26.78) * mm});
            skArc(sketch, "E624.MirrorCS", {"start": v(-33.24, 16.05) * mm, "mid": v(-34, 16.82) * mm, "end": v(-33.24, 17.58) * mm});
            skArc(sketch, "E625.MirrorCS", {"start": v(-33.24, 12.99) * mm, "mid": v(-34, 13.75) * mm, "end": v(-33.24, 14.52) * mm});
            skArc(sketch, "E626.MirrorCS", {"start": v(-33.24, 19.12) * mm, "mid": v(-34, 19.88) * mm, "end": v(-33.24, 20.65) * mm});
            skArc(sketch, "E627.MirrorCS", {"start": v(-47.2, -39.45) * mm, "mid": v(-47.96, -40.2) * mm, "end": v(-48.73, -39.45) * mm});
            skArc(sketch, "E628.MirrorCS", {"start": v(-41.06, -39.45) * mm, "mid": v(-41.83, -40.2) * mm, "end": v(-42.6, -39.45) * mm});
            skArc(sketch, "E629.MirrorCS", {"start": v(-50.26, -39.45) * mm, "mid": v(-51.03, -40.2) * mm, "end": v(-51.8, -39.45) * mm});
            skArc(sketch, "E630.MirrorCS", {"start": v(-53.33, -39.45) * mm, "mid": v(-54.1, -40.2) * mm, "end": v(-54.86, -39.45) * mm});
            skLineSegment(sketch, "E631.MirrorCS", {"start": v(-46.68, 24.43) * mm, "end": v(-46.7, 24.43) * mm});
            skArc(sketch, "E632.MirrorCS", {"start": v(-59.46, -39.45) * mm, "mid": v(-60.23, -40.2) * mm, "end": v(-61, -39.45) * mm});
            skArc(sketch, "E633.MirrorCS", {"start": v(-59.46, -14.8) * mm, "mid": v(-58.7, -14.05) * mm, "end": v(-57.93, -14.8) * mm});
            skArc(sketch, "E634.MirrorCS", {"start": v(-46.93, 24.42) * mm, "mid": v(-46.54, 24.63) * mm, "end": v(-46.37, 25.04) * mm});
            skArc(sketch, "E635.MirrorCS", {"start": v(-44.92, 24.42) * mm, "mid": v(-45.3, 24.63) * mm, "end": v(-45.48, 25.04) * mm});
            skLineSegment(sketch, "E636.MirrorCS", {"start": v(-36.47, -39.38) * mm, "end": v(-36.47, -39.45) * mm});
            skArc(sketch, "E637.MirrorCS", {"start": v(-38, -39.4) * mm, "mid": v(-38.77, -40.15) * mm, "end": v(-39.53, -39.4) * mm});
            skLineSegment(sketch, "E638.MirrorCS", {"start": v(-47.32, 40.63) * mm, "end": v(-47.51, 40.63) * mm});
            skArc(sketch, "E639.MirrorCS", {"start": v(-56.4, -39.45) * mm, "mid": v(-57.16, -40.2) * mm, "end": v(-57.93, -39.45) * mm});
            skLineSegment(sketch, "E640.MirrorCS", {"start": v(-44.34, 40.63) * mm, "end": v(-44.55, 40.63) * mm});
            skArc(sketch, "E641.MirrorCS", {"start": v(-44.13, -39.45) * mm, "mid": v(-44.9, -40.2) * mm, "end": v(-45.66, -39.45) * mm});
            skArc(sketch, "E642.MirrorCS", {"start": v(-35.4, -38.62) * mm, "mid": v(-35.81, -38.77) * mm, "end": v(-36.24, -38.65) * mm});
            skLineSegment(sketch, "E643.MirrorCS", {"start": v(-35.05, -4.6) * mm, "end": v(-33.25, -4.6) * mm});
            skArc(sketch, "E644.MirrorCS", {"start": v(-33.27, -34.52) * mm, "mid": v(-33.95, -36.77) * mm, "end": v(-35.4, -38.62) * mm});
            skLineSegment(sketch, "E645.MirrorCS", {"start": v(-63.4, 11.57) * mm, "end": v(-64.2, 11.11) * mm});
            skArc(sketch, "E646.MirrorCS", {"start": v(-36.24, -38.65) * mm, "mid": v(-36.4, -38.4) * mm, "end": v(-36.47, -38.12) * mm});
            skLineSegment(sketch, "E647.MirrorCS", {"start": v(-64.2, 11.11) * mm, "end": v(-64.2, 6.53) * mm});
            skLineSegment(sketch, "E648.MirrorCS", {"start": v(-63.4, 15.23) * mm, "end": v(-63.4, 11.57) * mm});
            skLineSegment(sketch, "E649.MirrorCS", {"start": v(-64.2, 6.53) * mm, "end": v(-64.99, 6.07) * mm});
            skLineSegment(sketch, "E650.MirrorCS", {"start": v(-46.7, 28.2) * mm, "end": v(-46.7, 28.2) * mm});
            skLineSegment(sketch, "E651.MirrorCS", {"start": v(-45.16, 28.2) * mm, "end": v(-45.16, 28.19) * mm});
            skArc(sketch, "E652.MirrorCS", {"start": v(-39.29, 2.98) * mm, "mid": v(-37.88, 3.8) * mm, "end": v(-36.38, 4.43) * mm});
            skLineSegment(sketch, "E653.MirrorCS", {"start": v(-64.99, 0.57) * mm, "end": v(-66.58, -0.35) * mm});
            skLineSegment(sketch, "E654.MirrorCS", {"start": v(-60.23, 17.07) * mm, "end": v(-63.4, 15.23) * mm});
            skLineSegment(sketch, "E655.MirrorCS", {"start": v(-66.58, -7.68) * mm, "end": v(-60.23, -11.34) * mm});
            skLineSegment(sketch, "E656.MirrorCS", {"start": v(-42.6, -16.96) * mm, "end": v(-42.6, -39.45) * mm});
            skLineSegment(sketch, "E657.MirrorCS", {"start": v(-66.58, -0.35) * mm, "end": v(-66.58, -7.68) * mm});
            skLineSegment(sketch, "E658.MirrorCS", {"start": v(-48.73, -15.67) * mm, "end": v(-48.73, -39.45) * mm});
            skLineSegment(sketch, "E659.MirrorCS", {"start": v(-38, -39.4) * mm, "end": v(-38, -18.87) * mm});
            skLineSegment(sketch, "E660.MirrorCS", {"start": v(-33.25, -4.6) * mm, "end": v(-33.27, -34.52) * mm});
            skArc(sketch, "E661.MirrorCS", {"start": v(-42.3, -6.86) * mm, "mid": v(-42.29, -1.48) * mm, "end": v(-39.29, 2.98) * mm});
            skLineSegment(sketch, "E662.MirrorCS", {"start": v(-36.47, -18.87) * mm, "end": v(-36.47, -38.12) * mm});
            skPoint(sketch, "E663.MirrorP", {"position": v(-45.92, 35.86) * mm});
            skArc(sketch, "E664.MirrorCS", {"start": v(-35.05, -4.6) * mm, "mid": v(-37.48, -9.6) * mm, "end": v(-42.3, -6.86) * mm});
            skLineSegment(sketch, "E665.MirrorCS", {"start": v(-59.46, -39.45) * mm, "end": v(-59.46, -14.8) * mm});
            skPoint(sketch, "E666.MirrorP", {"position": v(-63.4, -9.51) * mm});
            skLineSegment(sketch, "E667.MirrorCS", {"start": v(-44.13, -39.45) * mm, "end": v(-44.13, -16.96) * mm});
            skPoint(sketch, "E668.MirrorP", {"position": v(-33.24, -33.85) * mm});
            skPoint(sketch, "E669.MirrorP", {"position": v(-50.32, 35.64) * mm});
            skLineSegment(sketch, "E670.MirrorCS", {"start": v(-56.4, -39.45) * mm, "end": v(-56.4, -14.95) * mm});
            skLineSegment(sketch, "E671.MirrorCS", {"start": v(-45.66, -16.25) * mm, "end": v(-45.66, -39.45) * mm});
            skArc(sketch, "E672.MirrorCS", {"start": v(-44.92, 24.42) * mm, "mid": v(-45.94, 11.66) * mm, "end": v(-46.9, 24.42) * mm});
            skPoint(sketch, "E673.MirrorP", {"position": v(-50.29, 35.61) * mm});
            skArc(sketch, "E674.MirrorCS", {"start": v(-33.25, 8.6) * mm, "mid": v(-34.12, 6) * mm, "end": v(-36.38, 4.43) * mm});
            skLineSegment(sketch, "E675.MirrorCS", {"start": v(-54.86, -14.95) * mm, "end": v(-54.86, -39.45) * mm});
            skLineSegment(sketch, "E676.MirrorCS", {"start": v(-64.99, 6.07) * mm, "end": v(-64.99, 0.57) * mm});
            skLineSegment(sketch, "E677.MirrorCS", {"start": v(-47.2, -39.45) * mm, "end": v(-47.2, -16.25) * mm});
            skPoint(sketch, "E678.MirrorP", {"position": v(-34.53, -40.82) * mm});
            skLineSegment(sketch, "E679.MirrorCS", {"start": v(-41.06, -39.45) * mm, "end": v(-41.06, -17.83) * mm});
            skLineSegment(sketch, "E680.MirrorCS", {"start": v(-50.26, -39.45) * mm, "end": v(-50.26, -15.67) * mm});
            skLineSegment(sketch, "E681.MirrorCS", {"start": v(-51.8, -15.26) * mm, "end": v(-51.8, -39.45) * mm});
            skLineSegment(sketch, "E682.MirrorCS", {"start": v(-57.93, -14.8) * mm, "end": v(-57.93, -39.45) * mm});
            skLineSegment(sketch, "E683.MirrorCS", {"start": v(-53.33, -39.45) * mm, "end": v(-53.33, -15.26) * mm});
            skLineSegment(sketch, "E684", {"start": v(-80.86, 45.4) * mm, "end": v(-39.59, 45.4) * mm});
            skArc(sketch, "E685", {"start": v(-55.92, 21.44) * mm, "mid": v(-60.22, 22.69) * mm, "end": v(-64.49, 21.31) * mm});
            skArc(sketch, "E686", {"start": v(-58.64, 27.67) * mm, "mid": v(-58.89, 27.1) * mm, "end": v(-59, 26.5) * mm});
            skArc(sketch, "E687", {"start": v(-58.9, 25.53) * mm, "mid": v(-58.54, 24.84) * mm, "end": v(-57.84, 24.51) * mm});
            skArc(sketch, "E688", {"start": v(-57.84, 29.06) * mm, "mid": v(-58.2, 29.02) * mm, "end": v(-58.54, 28.94) * mm});
            skArc(sketch, "E689", {"start": v(-58.54, 28.94) * mm, "mid": v(-58.96, 28.77) * mm, "end": v(-59.35, 28.51) * mm});
            skArc(sketch, "E690", {"start": v(-59.35, 28.51) * mm, "mid": v(-59.7, 28.12) * mm, "end": v(-59.95, 27.65) * mm});
            skArc(sketch, "E691", {"start": v(-59.95, 27.65) * mm, "mid": v(-60.11, 27.09) * mm, "end": v(-60.17, 26.5) * mm});
            skArc(sketch, "E692", {"start": v(-60.17, 26.5) * mm, "mid": v(-60.17, 26.5) * mm, "end": v(-60.17, 26.5) * mm});
            skArc(sketch, "E693", {"start": v(-60.14, 25.7) * mm, "mid": v(-60.07, 25.3) * mm, "end": v(-59.94, 24.94) * mm});
            skArc(sketch, "E694", {"start": v(-59.94, 24.94) * mm, "mid": v(-59.8, 24.65) * mm, "end": v(-59.62, 24.38) * mm});
            skArc(sketch, "E695", {"start": v(-59.62, 24.38) * mm, "mid": v(-59.36, 24.12) * mm, "end": v(-59.07, 23.9) * mm});
            skArc(sketch, "E696", {"start": v(-59.07, 23.9) * mm, "mid": v(-58.72, 23.74) * mm, "end": v(-58.35, 23.64) * mm});
            skArc(sketch, "E697", {"start": v(-58.35, 23.64) * mm, "mid": v(-58.12, 23.6) * mm, "end": v(-57.88, 23.57) * mm});
            skArc(sketch, "E698", {"start": v(-57.88, 23.57) * mm, "mid": v(-57.86, 23.57) * mm, "end": v(-57.84, 23.57) * mm});
            skLineSegment(sketch, "E699", {"start": v(-57.65, 28.11) * mm, "end": v(-57.65, 28.12) * mm});
            skLineSegment(sketch, "E700", {"start": v(-57.64, 24.5) * mm, "end": v(-57.64, 24.5) * mm});
            skLineSegment(sketch, "E701.trimOffspring", {"start": v(-57.84, 28.1) * mm, "end": v(-57.84, 29.06) * mm});
            skLineSegment(sketch, "E702", {"start": v(-57.84, 24.04) * mm, "end": v(-57.84, 23.57) * mm});
            skArc(sketch, "E703.trimOffspring", {"start": v(-57.64, 23.56) * mm, "mid": v(-57.63, 23.56) * mm, "end": v(-57.63, 23.56) * mm});
            skLineSegment(sketch, "E704.trimOffspring", {"start": v(-57.84, 24.51) * mm, "end": v(-57.84, 24.04) * mm});
            skArc(sketch, "E705.trimOffspring", {"start": v(-57.84, 28.1) * mm, "mid": v(-58.27, 27.95) * mm, "end": v(-58.64, 27.67) * mm});
            skPoint(sketch, "E706.orphan", {"position": v(-59.01, 26.24) * mm});
            skLineSegment(sketch, "E707", {"start": v(-57.65, 28.12) * mm, "end": v(-57.65, 28.11) * mm});
            skArc(sketch, "E708.MirrorCS", {"start": v(-57.46, 28.1) * mm, "mid": v(-57.02, 27.96) * mm, "end": v(-56.66, 27.68) * mm});
            skArc(sketch, "E709.MirrorCS", {"start": v(-56.66, 27.68) * mm, "mid": v(-56.4, 27.12) * mm, "end": v(-56.28, 26.52) * mm});
            skArc(sketch, "E710.MirrorCS", {"start": v(-56.37, 25.54) * mm, "mid": v(-56.73, 24.85) * mm, "end": v(-57.43, 24.51) * mm});
            skArc(sketch, "E711.MirrorCS", {"start": v(-57.38, 23.57) * mm, "mid": v(-57.4, 23.57) * mm, "end": v(-57.42, 23.57) * mm});
            skArc(sketch, "E712.MirrorCS", {"start": v(-56.9, 23.64) * mm, "mid": v(-57.14, 23.6) * mm, "end": v(-57.38, 23.57) * mm});
            skArc(sketch, "E713.MirrorCS", {"start": v(-56.2, 23.92) * mm, "mid": v(-56.54, 23.75) * mm, "end": v(-56.9, 23.64) * mm});
            skArc(sketch, "E714.MirrorCS", {"start": v(-55.64, 24.4) * mm, "mid": v(-55.9, 24.14) * mm, "end": v(-56.2, 23.92) * mm});
            skArc(sketch, "E715.MirrorCS", {"start": v(-55.33, 24.96) * mm, "mid": v(-55.46, 24.67) * mm, "end": v(-55.64, 24.4) * mm});
            skArc(sketch, "E716.MirrorCS", {"start": v(-55.14, 25.72) * mm, "mid": v(-55.2, 25.33) * mm, "end": v(-55.33, 24.96) * mm});
            skArc(sketch, "E717.MirrorCS", {"start": v(-55.11, 26.53) * mm, "mid": v(-55.11, 26.53) * mm, "end": v(-55.11, 26.52) * mm});
            skArc(sketch, "E718.MirrorCS", {"start": v(-55.35, 27.67) * mm, "mid": v(-55.18, 27.11) * mm, "end": v(-55.11, 26.53) * mm});
            skArc(sketch, "E719.MirrorCS", {"start": v(-55.96, 28.53) * mm, "mid": v(-55.6, 28.14) * mm, "end": v(-55.35, 27.67) * mm});
            skArc(sketch, "E720.MirrorCS", {"start": v(-56.77, 28.95) * mm, "mid": v(-56.34, 28.78) * mm, "end": v(-55.96, 28.53) * mm});
            skArc(sketch, "E721.MirrorCS", {"start": v(-57.46, 29.06) * mm, "mid": v(-57.12, 29.02) * mm, "end": v(-56.77, 28.95) * mm});
            skLineSegment(sketch, "E722.MirrorCS", {"start": v(-57.46, 28.1) * mm, "end": v(-57.46, 29.06) * mm});
            skLineSegment(sketch, "E723.MirrorCS", {"start": v(-57.43, 24.51) * mm, "end": v(-57.42, 24.04) * mm});
            skLineSegment(sketch, "E724.MirrorCS", {"start": v(-57.42, 24.04) * mm, "end": v(-57.42, 23.57) * mm});
            skArc(sketch, "E725", {"start": v(-57.64, 24.5) * mm, "mid": v(-57.63, 24.5) * mm, "end": v(-57.63, 24.5) * mm});
            skLineSegment(sketch, "E726.0", {"start": v(-60.18, 26.12) * mm, "end": v(-59, 26.13) * mm});
            skLineSegment(sketch, "E727.0", {"start": v(-60.18, 26.5) * mm, "end": v(-59, 26.5) * mm});
            skLineSegment(sketch, "E728.trimOffspring", {"start": v(-56.28, 26.52) * mm, "end": v(-55.1, 26.52) * mm});
            skPoint(sketch, "E729.orphan", {"position": v(-57.64, 26.31) * mm});
            skLineSegment(sketch, "E730.trimOffspring", {"start": v(-56.27, 26.14) * mm, "end": v(-55.1, 26.15) * mm});
            skPoint(sketch, "E731.MirrorCS.end.orphan", {"position": v(-57.63, 24.5) * mm});
            skPoint(sketch, "E731.MirrorCS.start.orphan", {"position": v(-57.43, 24.51) * mm});
            skPoint(sketch, "E732.MirrorCS.end.orphan", {"position": v(-57.25, 23.56) * mm});
            skPoint(sketch, "E732.MirrorCS.start.orphan", {"position": v(-57.04, 23.57) * mm});
            skPoint(sketch, "E733.orphan", {"position": v(-57.65, 29.06) * mm});
            skPoint(sketch, "E734.MirrorCS.end.orphan", {"position": v(-57.46, 28.1) * mm});
            skArc(sketch, "E735.trimOffspring", {"start": v(-60.17, 26.12) * mm, "mid": v(-60.16, 25.9) * mm, "end": v(-60.14, 25.7) * mm});
            skArc(sketch, "E736.trimOffspring", {"start": v(-59, 26.13) * mm, "mid": v(-58.98, 25.82) * mm, "end": v(-58.9, 25.53) * mm});
            skArc(sketch, "E737.trimOffspring", {"start": v(-56.27, 26.14) * mm, "mid": v(-56.3, 25.84) * mm, "end": v(-56.37, 25.54) * mm});
            skArc(sketch, "E738.trimOffspring", {"start": v(-55.1, 26.15) * mm, "mid": v(-55.12, 25.93) * mm, "end": v(-55.14, 25.72) * mm});
            skText(sketch, "E739", { "text": "X", "fontName": "OpenSans-Bold.ttf"});
            skLineSegment(sketch, "E740", {"start": v(-55.92, 20.18) * mm, "end": v(-55.92, 21.44) * mm});
            skLineSegment(sketch, "E741", {"start": v(-55.92, 21.44) * mm, "end": v(-55.92, 20.18) * mm});
            skCircle(sketch, "E742", {"center": v(-57.64, 26.31) * mm, "radius": 0.65 * mm});
            skArc(sketch, "E743.0", {"start": v(-55.92, 20.18) * mm, "mid": v(-60.23, 21.67) * mm, "end": v(-64.49, 20.03) * mm});
            skLineSegment(sketch, "E744", {"start": v(-64.49, 21.31) * mm, "end": v(-64.49, 20.03) * mm});
            skLineSegment(sketch, "E745.trimOffspring", {"start": v(-39.53, -17.83) * mm, "end": v(-39.53, -39.4) * mm});
            skArc(sketch, "E746.MirrorCS", {"start": v(-56.4, -14.95) * mm, "mid": v(-55.63, -14.2) * mm, "end": v(-54.86, -14.95) * mm});
            skArc(sketch, "E747.MirrorCS", {"start": v(-50.26, -15.67) * mm, "mid": v(-49.5, -14.9) * mm, "end": v(-48.73, -15.67) * mm});
            skArc(sketch, "E748.MirrorCS", {"start": v(-38, -18.87) * mm, "mid": v(-37.23, -18.11) * mm, "end": v(-36.47, -18.87) * mm});
            skArc(sketch, "E749.MirrorCS", {"start": v(-41.06, -17.83) * mm, "mid": v(-40.3, -17.07) * mm, "end": v(-39.53, -17.83) * mm});
            skArc(sketch, "E750.MirrorCS", {"start": v(-44.13, -16.96) * mm, "mid": v(-43.36, -16.2) * mm, "end": v(-42.6, -16.96) * mm});
            skArc(sketch, "E751.MirrorCS", {"start": v(-47.2, -16.25) * mm, "mid": v(-46.43, -15.5) * mm, "end": v(-45.66, -16.25) * mm});
            skArc(sketch, "E752.MirrorCS", {"start": v(-53.33, -15.26) * mm, "mid": v(-52.56, -14.5) * mm, "end": v(-51.8, -15.26) * mm});
            skArc(sketch, "E753.MirrorCS", {"start": v(-84.21, -38.65) * mm, "mid": v(-84.05, -38.4) * mm, "end": v(-83.98, -38.12) * mm});
            skArc(sketch, "E754.MirrorCS", {"start": v(-82.45, -18.87) * mm, "mid": v(-83.22, -18.11) * mm, "end": v(-83.98, -18.87) * mm});
            skArc(sketch, "E755.MirrorCS", {"start": v(-85.06, -38.62) * mm, "mid": v(-84.64, -38.77) * mm, "end": v(-84.21, -38.65) * mm});
            skLineSegment(sketch, "E756.MirrorCS", {"start": v(-83.98, -39.38) * mm, "end": v(-83.98, -39.45) * mm});
            skArc(sketch, "E757.MirrorCS", {"start": v(-73.25, -16.25) * mm, "mid": v(-74.02, -15.5) * mm, "end": v(-74.79, -16.25) * mm});
            skArc(sketch, "E758.MirrorCS", {"start": v(-79.39, -17.83) * mm, "mid": v(-80.15, -17.07) * mm, "end": v(-80.92, -17.83) * mm});
            skArc(sketch, "E759.MirrorCS", {"start": v(-73.25, -39.45) * mm, "mid": v(-72.49, -40.2) * mm, "end": v(-71.72, -39.45) * mm});
            skArc(sketch, "E760.MirrorCS", {"start": v(-79.39, -39.45) * mm, "mid": v(-78.62, -40.2) * mm, "end": v(-77.85, -39.45) * mm});
            skArc(sketch, "E761.MirrorCS", {"start": v(-62.52, -14.8) * mm, "mid": v(-61.76, -14.05) * mm, "end": v(-61, -14.8) * mm});
            skLineSegment(sketch, "E762.MirrorCS", {"start": v(-80.92, -17.83) * mm, "end": v(-80.92, -39.4) * mm});
            skLineSegment(sketch, "E763.MirrorCS", {"start": v(-74.79, -16.25) * mm, "end": v(-74.79, -39.45) * mm});
            skLineSegment(sketch, "E764.MirrorCS", {"start": v(-68.66, -15.26) * mm, "end": v(-68.66, -39.45) * mm});
            skLineSegment(sketch, "E765.MirrorCS", {"start": v(-65.6, -14.95) * mm, "end": v(-65.6, -39.45) * mm});
            skLineSegment(sketch, "E766.MirrorCS", {"start": v(-61, -39.45) * mm, "end": v(-61, -14.8) * mm});
            skArc(sketch, "E767.MirrorCS", {"start": v(-70.19, -15.67) * mm, "mid": v(-70.96, -14.9) * mm, "end": v(-71.72, -15.67) * mm});
            skLineSegment(sketch, "E768.MirrorCS", {"start": v(-62.52, -14.8) * mm, "end": v(-62.52, -39.45) * mm});
            skLineSegment(sketch, "E769.MirrorCS", {"start": v(-82.45, -39.4) * mm, "end": v(-82.45, -18.87) * mm});
            skLineSegment(sketch, "E770.MirrorCS", {"start": v(-83.98, -18.87) * mm, "end": v(-83.98, -38.12) * mm});
            skArc(sketch, "E771.MirrorCS", {"start": v(-61, -14.8) * mm, "mid": v(-61.76, -14.05) * mm, "end": v(-62.52, -14.8) * mm});
            skLineSegment(sketch, "E772.MirrorCS", {"start": v(-71.72, -15.67) * mm, "end": v(-71.72, -39.45) * mm});
            skLineSegment(sketch, "E773.MirrorCS", {"start": v(-79.39, -39.45) * mm, "end": v(-79.39, -17.83) * mm});
            skArc(sketch, "E774.MirrorCS", {"start": v(-76.32, -39.45) * mm, "mid": v(-75.55, -40.2) * mm, "end": v(-74.79, -39.45) * mm});
            skLineSegment(sketch, "E775.MirrorCS", {"start": v(-73.25, -39.45) * mm, "end": v(-73.25, -16.25) * mm});
            skArc(sketch, "E776.MirrorCS", {"start": v(-67.12, -39.45) * mm, "mid": v(-66.36, -40.2) * mm, "end": v(-65.6, -39.45) * mm});
            skLineSegment(sketch, "E777.MirrorCS", {"start": v(-76.32, -39.45) * mm, "end": v(-76.32, -16.96) * mm});
            skArc(sketch, "E778.MirrorCS", {"start": v(-64.06, -39.45) * mm, "mid": v(-63.3, -40.2) * mm, "end": v(-62.52, -39.45) * mm});
            skLineSegment(sketch, "E779.MirrorCS", {"start": v(-70.19, -39.45) * mm, "end": v(-70.19, -15.67) * mm});
            skLineSegment(sketch, "E780.MirrorCS", {"start": v(-64.06, -39.45) * mm, "end": v(-64.06, -14.95) * mm});
            skLineSegment(sketch, "E781.MirrorCS", {"start": v(-67.12, -39.45) * mm, "end": v(-67.12, -15.26) * mm});
            skArc(sketch, "E782.MirrorCS", {"start": v(-64.06, -14.95) * mm, "mid": v(-64.82, -14.2) * mm, "end": v(-65.6, -14.95) * mm});
            skLineSegment(sketch, "E783.MirrorCS", {"start": v(-77.85, -16.96) * mm, "end": v(-77.85, -39.45) * mm});
            skArc(sketch, "E784.MirrorCS", {"start": v(-82.45, -39.4) * mm, "mid": v(-81.69, -40.15) * mm, "end": v(-80.92, -39.4) * mm});
            skArc(sketch, "E785.MirrorCS", {"start": v(-70.19, -39.45) * mm, "mid": v(-69.42, -40.2) * mm, "end": v(-68.66, -39.45) * mm});
            skArc(sketch, "E786.MirrorCS", {"start": v(-76.32, -16.96) * mm, "mid": v(-77.09, -16.2) * mm, "end": v(-77.85, -16.96) * mm});
            skArc(sketch, "E787.MirrorCS", {"start": v(-67.12, -15.26) * mm, "mid": v(-67.89, -14.5) * mm, "end": v(-68.66, -15.26) * mm});
            skPoint(sketch, "E788.MirrorP", {"position": v(-85.92, -40.82) * mm});
            skLineSegment(sketch, "E789.0", {"start": v(-115.74, -7.68) * mm, "end": v(-122.09, -11.34) * mm});
            skLineSegment(sketch, "E789.4", {"start": v(-117.32, 0.57) * mm, "end": v(-115.74, -0.35) * mm});
            skLineSegment(sketch, "E789.5", {"start": v(-115.74, -0.35) * mm, "end": v(-115.74, -7.68) * mm});
            skPoint(sketch, "E789.0.midPoint", {"position": v(-118.91, -9.51) * mm});
            skLineSegment(sketch, "E790.4", {"start": v(-118.12, 6.53) * mm, "end": v(-117.32, 6.07) * mm});
            skLineSegment(sketch, "E790.5", {"start": v(-117.32, 6.07) * mm, "end": v(-117.32, 0.57) * mm});
            skLineSegment(sketch, "E791.4", {"start": v(-118.91, 11.57) * mm, "end": v(-118.12, 11.11) * mm});
            skLineSegment(sketch, "E791.5", {"start": v(-118.12, 11.11) * mm, "end": v(-118.12, 6.53) * mm});
            skLineSegment(sketch, "E792.4", {"start": v(-122.09, 17.07) * mm, "end": v(-118.91, 15.23) * mm});
            skLineSegment(sketch, "E792.5", {"start": v(-118.91, 15.23) * mm, "end": v(-118.91, 11.57) * mm});
            skLineSegment(sketch, "E793.left", {"start": v(-149.07, 37.51) * mm, "end": v(-149.07, 35.98) * mm});
            skArc(sketch, "E794.filletArc", {"start": v(-142.72, 45.4) * mm, "mid": v(-147.21, 43.53) * mm, "end": v(-149.07, 39.04) * mm});
            skArc(sketch, "E795.filletArc", {"start": v(-149.04, -34.52) * mm, "mid": v(-148.36, -36.77) * mm, "end": v(-146.92, -38.62) * mm});
            skLineSegment(sketch, "E796", {"start": v(-145.9, 39.04) * mm, "end": v(-145.9, 40.63) * mm});
            skLineSegment(sketch, "E797", {"start": v(-145.9, 40.63) * mm, "end": v(-137.98, 40.63) * mm});
            skLineSegment(sketch, "E798", {"start": v(-126.85, 40.63) * mm, "end": v(-126.85, 39.04) * mm});
            skLineSegment(sketch, "E799", {"start": v(-145.9, 39.04) * mm, "end": v(-137.77, 39.04) * mm});
            skLineSegment(sketch, "E800.MirrorCS", {"start": v(-135.62, 28.2) * mm, "end": v(-135.62, 28.2) * mm});
            skLineSegment(sketch, "E801.MirrorCS", {"start": v(-137.15, 28.2) * mm, "end": v(-137.15, 28.19) * mm});
            skLineSegment(sketch, "E802.MirrorCS", {"start": v(-135.94, 35.86) * mm, "end": v(-136.83, 35.86) * mm});
            skLineSegment(sketch, "E803", {"start": v(-135.63, 24.43) * mm, "end": v(-135.62, 24.43) * mm});
            skLineSegment(sketch, "E804.0", {"start": v(-136.83, 35.86) * mm, "end": v(-136.83, 25.04) * mm});
            skLineSegment(sketch, "E805.0", {"start": v(-135.94, 35.86) * mm, "end": v(-135.94, 25.04) * mm});
            skArc(sketch, "E806", {"start": v(-137.39, 24.42) * mm, "mid": v(-136.37, 11.66) * mm, "end": v(-135.4, 24.42) * mm});
            skArc(sketch, "E807", {"start": v(-149.07, 9.92) * mm, "mid": v(-148.32, 10.69) * mm, "end": v(-149.07, 11.45) * mm});
            skArc(sketch, "E808", {"start": v(-149.07, 12.99) * mm, "mid": v(-148.32, 13.75) * mm, "end": v(-149.07, 14.52) * mm});
            skArc(sketch, "E809", {"start": v(-149.07, 16.05) * mm, "mid": v(-148.32, 16.82) * mm, "end": v(-149.07, 17.58) * mm});
            skArc(sketch, "E810", {"start": v(-149.07, 19.12) * mm, "mid": v(-148.32, 19.88) * mm, "end": v(-149.07, 20.65) * mm});
            skArc(sketch, "E811", {"start": v(-149.07, 22.18) * mm, "mid": v(-148.32, 22.95) * mm, "end": v(-149.07, 23.71) * mm});
            skArc(sketch, "E812", {"start": v(-149.07, 25.25) * mm, "mid": v(-148.32, 26.01) * mm, "end": v(-149.07, 26.78) * mm});
            skArc(sketch, "E813", {"start": v(-149.07, 28.31) * mm, "mid": v(-148.32, 29.08) * mm, "end": v(-149.07, 29.85) * mm});
            skArc(sketch, "E814", {"start": v(-149.07, 31.38) * mm, "mid": v(-148.32, 32.15) * mm, "end": v(-149.07, 32.91) * mm});
            skArc(sketch, "E815", {"start": v(-149.07, 34.44) * mm, "mid": v(-148.32, 35.21) * mm, "end": v(-149.07, 35.98) * mm});
            skArc(sketch, "E816", {"start": v(-149.07, 37.51) * mm, "mid": v(-148.32, 38.28) * mm, "end": v(-149.07, 39.04) * mm});
            skLineSegment(sketch, "E817.trimOffspring", {"start": v(-149.07, 12.99) * mm, "end": v(-149.07, 11.45) * mm});
            skLineSegment(sketch, "E818.trimOffspring", {"start": v(-149.07, 16.05) * mm, "end": v(-149.07, 14.52) * mm});
            skLineSegment(sketch, "E819.trimOffspring", {"start": v(-149.07, 19.12) * mm, "end": v(-149.07, 17.58) * mm});
            skLineSegment(sketch, "E820.trimOffspring", {"start": v(-149.07, 22.18) * mm, "end": v(-149.07, 20.65) * mm});
            skLineSegment(sketch, "E821.trimOffspring", {"start": v(-149.07, 25.25) * mm, "end": v(-149.07, 23.71) * mm});
            skLineSegment(sketch, "E822.trimOffspring", {"start": v(-149.07, 28.31) * mm, "end": v(-149.07, 26.78) * mm});
            skLineSegment(sketch, "E823.trimOffspring", {"start": v(-149.07, 31.38) * mm, "end": v(-149.07, 29.85) * mm});
            skLineSegment(sketch, "E824.trimOffspring", {"start": v(-149.07, 34.44) * mm, "end": v(-149.07, 32.91) * mm});
            skPoint(sketch, "E825.orphan", {"position": v(-136.39, 35.86) * mm});
            skLineSegment(sketch, "E826.trimOffspring", {"start": v(-134.8, 40.63) * mm, "end": v(-126.85, 40.63) * mm});
            skLineSegment(sketch, "E827", {"start": v(-137.98, 40.63) * mm, "end": v(-137.77, 40.63) * mm});
            skArc(sketch, "E828.MirrorCS", {"start": v(-137.77, 40.63) * mm, "mid": v(-136.38, 41.44) * mm, "end": v(-134.99, 40.63) * mm});
            skArc(sketch, "E829.MirrorCS", {"start": v(-134.99, 39.04) * mm, "mid": v(-136.38, 38.24) * mm, "end": v(-137.77, 39.04) * mm});
            skLineSegment(sketch, "E830.trimOffspring", {"start": v(-134.99, 39.04) * mm, "end": v(-131.36, 39.04) * mm});
            skLineSegment(sketch, "E831.trimOffspring", {"start": v(-134.99, 40.63) * mm, "end": v(-134.8, 40.63) * mm});
            skLineSegment(sketch, "E832.trimOffspring", {"start": v(-130.37, 39.04) * mm, "end": v(-126.85, 39.04) * mm});
            skArc(sketch, "E833", {"start": v(-132, 35.64) * mm, "mid": v(-131.04, 37.22) * mm, "end": v(-131.36, 39.04) * mm});
            skArc(sketch, "E834.0", {"start": v(-130.48, 36.12) * mm, "mid": v(-130.1, 37.57) * mm, "end": v(-130.37, 39.04) * mm});
            skPoint(sketch, "E835.start.orphan", {"position": v(-132, 35.64) * mm});
            skArc(sketch, "E836.MirrorCS", {"start": v(-132, 35.64) * mm, "mid": v(-130.67, 30.6) * mm, "end": v(-130.33, 35.8) * mm});
            skPoint(sketch, "E837.orphan", {"position": v(-132.02, 35.61) * mm});
            skArc(sketch, "E838", {"start": v(-137.39, 24.42) * mm, "mid": v(-137, 24.63) * mm, "end": v(-136.83, 25.04) * mm});
            skArc(sketch, "E839.MirrorCS", {"start": v(-135.39, 24.42) * mm, "mid": v(-135.77, 24.63) * mm, "end": v(-135.94, 25.04) * mm});
            skArc(sketch, "E840", {"start": v(-130.48, 36.12) * mm, "mid": v(-130.48, 35.92) * mm, "end": v(-130.33, 35.8) * mm});
            skArc(sketch, "E841", {"start": v(-122.85, -39.45) * mm, "mid": v(-122.09, -40.2) * mm, "end": v(-121.32, -39.45) * mm});
            skArc(sketch, "E842.MirrorCS", {"start": v(-149.06, 8.6) * mm, "mid": v(-148.2, 6) * mm, "end": v(-145.93, 4.43) * mm});
            skArc(sketch, "E843.MirrorCS", {"start": v(-143.02, 2.98) * mm, "mid": v(-144.43, 3.8) * mm, "end": v(-145.93, 4.43) * mm});
            skArc(sketch, "E844.MirrorCS", {"start": v(-140, -6.86) * mm, "mid": v(-140.02, -1.48) * mm, "end": v(-143.02, 2.98) * mm});
            skArc(sketch, "E845.MirrorCS", {"start": v(-147.27, -4.6) * mm, "mid": v(-144.83, -9.6) * mm, "end": v(-140, -6.86) * mm});
            skLineSegment(sketch, "E846.MirrorCS", {"start": v(-147.27, -4.6) * mm, "end": v(-149.06, -4.6) * mm});
            skLineSegment(sketch, "E847.MirrorCS", {"start": v(-149.06, -4.6) * mm, "end": v(-149.04, -34.52) * mm});
            skLineSegment(sketch, "E848", {"start": v(-149.06, 8.6) * mm, "end": v(-149.07, 9.92) * mm});
            skArc(sketch, "E849.MirrorCS", {"start": v(-121.32, -39.45) * mm, "mid": v(-122.09, -40.2) * mm, "end": v(-122.85, -39.45) * mm});
            skLineSegment(sketch, "E850.MirrorCS", {"start": v(-125.26, 11.57) * mm, "end": v(-126.05, 11.11) * mm});
            skLineSegment(sketch, "E851.MirrorCS", {"start": v(-126.05, 11.11) * mm, "end": v(-126.05, 6.53) * mm});
            skLineSegment(sketch, "E852.MirrorCS", {"start": v(-125.26, 15.23) * mm, "end": v(-125.26, 11.57) * mm});
            skLineSegment(sketch, "E853.MirrorCS", {"start": v(-126.05, 6.53) * mm, "end": v(-126.85, 6.07) * mm});
            skLineSegment(sketch, "E854.MirrorCS", {"start": v(-126.85, 0.57) * mm, "end": v(-128.44, -0.35) * mm});
            skLineSegment(sketch, "E855.MirrorCS", {"start": v(-122.09, 17.07) * mm, "end": v(-125.26, 15.23) * mm});
            skLineSegment(sketch, "E856.MirrorCS", {"start": v(-128.44, -7.68) * mm, "end": v(-122.09, -11.34) * mm});
            skLineSegment(sketch, "E857.MirrorCS", {"start": v(-128.44, -0.35) * mm, "end": v(-128.44, -7.68) * mm});
            skPoint(sketch, "E858.MirrorP", {"position": v(-125.26, -9.51) * mm});
            skLineSegment(sketch, "E859.MirrorCS", {"start": v(-126.85, 6.07) * mm, "end": v(-126.85, 0.57) * mm});
            skLineSegment(sketch, "E860", {"start": v(-142.72, 45.4) * mm, "end": v(-101.45, 45.4) * mm});
            skArc(sketch, "E861", {"start": v(-117.9, 21) * mm, "mid": v(-122.2, 22.24) * mm, "end": v(-126.46, 20.87) * mm});
            skArc(sketch, "E862", {"start": v(-120.61, 27.23) * mm, "mid": v(-120.86, 26.66) * mm, "end": v(-120.98, 26.06) * mm});
            skArc(sketch, "E863", {"start": v(-120.88, 25.08) * mm, "mid": v(-120.51, 24.4) * mm, "end": v(-119.81, 24.07) * mm});
            skArc(sketch, "E864", {"start": v(-119.82, 28.61) * mm, "mid": v(-120.17, 28.57) * mm, "end": v(-120.5, 28.5) * mm});
            skArc(sketch, "E865", {"start": v(-120.5, 28.5) * mm, "mid": v(-120.94, 28.33) * mm, "end": v(-121.32, 28.07) * mm});
            skArc(sketch, "E866", {"start": v(-121.32, 28.07) * mm, "mid": v(-121.67, 27.68) * mm, "end": v(-121.92, 27.2) * mm});
            skArc(sketch, "E867", {"start": v(-121.92, 27.2) * mm, "mid": v(-122.08, 26.64) * mm, "end": v(-122.14, 26.06) * mm});
            skArc(sketch, "E868", {"start": v(-122.14, 26.06) * mm, "mid": v(-122.14, 26.06) * mm, "end": v(-122.14, 26.06) * mm});
            skArc(sketch, "E869", {"start": v(-122.1, 25.25) * mm, "mid": v(-122.04, 24.87) * mm, "end": v(-121.92, 24.5) * mm});
            skArc(sketch, "E870", {"start": v(-121.92, 24.5) * mm, "mid": v(-121.78, 24.2) * mm, "end": v(-121.6, 23.94) * mm});
            skArc(sketch, "E871", {"start": v(-121.6, 23.94) * mm, "mid": v(-121.34, 23.67) * mm, "end": v(-121.04, 23.46) * mm});
            skArc(sketch, "E872", {"start": v(-121.04, 23.46) * mm, "mid": v(-120.7, 23.3) * mm, "end": v(-120.33, 23.2) * mm});
            skArc(sketch, "E873", {"start": v(-120.33, 23.2) * mm, "mid": v(-120.1, 23.15) * mm, "end": v(-119.85, 23.13) * mm});
            skArc(sketch, "E874", {"start": v(-119.85, 23.13) * mm, "mid": v(-119.83, 23.12) * mm, "end": v(-119.81, 23.12) * mm});
            skLineSegment(sketch, "E875", {"start": v(-119.62, 27.67) * mm, "end": v(-119.62, 27.67) * mm});
            skLineSegment(sketch, "E876", {"start": v(-119.61, 24.06) * mm, "end": v(-119.61, 24.05) * mm});
            skLineSegment(sketch, "E877.trimOffspring", {"start": v(-119.81, 27.65) * mm, "end": v(-119.82, 28.62) * mm});
            skLineSegment(sketch, "E878", {"start": v(-119.81, 23.6) * mm, "end": v(-119.81, 23.12) * mm});
            skArc(sketch, "E879.trimOffspring", {"start": v(-119.61, 23.12) * mm, "mid": v(-119.6, 23.12) * mm, "end": v(-119.6, 23.12) * mm});
            skLineSegment(sketch, "E880.trimOffspring", {"start": v(-119.81, 24.07) * mm, "end": v(-119.81, 23.6) * mm});
            skArc(sketch, "E881.trimOffspring", {"start": v(-119.81, 27.65) * mm, "mid": v(-120.25, 27.5) * mm, "end": v(-120.61, 27.23) * mm});
            skPoint(sketch, "E882.orphan", {"position": v(-120.99, 25.8) * mm});
            skArc(sketch, "E883.MirrorCS", {"start": v(-119.43, 27.65) * mm, "mid": v(-119, 27.51) * mm, "end": v(-118.63, 27.24) * mm});
            skArc(sketch, "E884.MirrorCS", {"start": v(-118.63, 27.24) * mm, "mid": v(-118.38, 26.68) * mm, "end": v(-118.25, 26.07) * mm});
            skArc(sketch, "E885.MirrorCS", {"start": v(-118.34, 25.1) * mm, "mid": v(-118.7, 24.4) * mm, "end": v(-119.4, 24.07) * mm});
            skArc(sketch, "E886.MirrorCS", {"start": v(-119.35, 23.13) * mm, "mid": v(-119.37, 23.13) * mm, "end": v(-119.39, 23.13) * mm});
            skArc(sketch, "E887.MirrorCS", {"start": v(-118.88, 23.2) * mm, "mid": v(-119.11, 23.15) * mm, "end": v(-119.35, 23.13) * mm});
            skArc(sketch, "E888.MirrorCS", {"start": v(-118.17, 23.47) * mm, "mid": v(-118.5, 23.3) * mm, "end": v(-118.88, 23.2) * mm});
            skArc(sketch, "E889.MirrorCS", {"start": v(-117.62, 23.96) * mm, "mid": v(-117.87, 23.7) * mm, "end": v(-118.17, 23.47) * mm});
            skArc(sketch, "E890.MirrorCS", {"start": v(-117.3, 24.52) * mm, "mid": v(-117.44, 24.23) * mm, "end": v(-117.62, 23.96) * mm});
            skArc(sketch, "E891.MirrorCS", {"start": v(-117.11, 25.27) * mm, "mid": v(-117.18, 24.89) * mm, "end": v(-117.3, 24.52) * mm});
            skArc(sketch, "E892.MirrorCS", {"start": v(-117.09, 26.08) * mm, "mid": v(-117.09, 26.08) * mm, "end": v(-117.09, 26.08) * mm});
            skArc(sketch, "E893.MirrorCS", {"start": v(-117.32, 27.23) * mm, "mid": v(-117.15, 26.67) * mm, "end": v(-117.09, 26.08) * mm});
            skArc(sketch, "E894.MirrorCS", {"start": v(-117.93, 28.08) * mm, "mid": v(-117.57, 27.7) * mm, "end": v(-117.32, 27.23) * mm});
            skArc(sketch, "E895.MirrorCS", {"start": v(-118.74, 28.5) * mm, "mid": v(-118.31, 28.34) * mm, "end": v(-117.93, 28.08) * mm});
            skArc(sketch, "E896.MirrorCS", {"start": v(-119.44, 28.61) * mm, "mid": v(-119.09, 28.58) * mm, "end": v(-118.74, 28.5) * mm});
            skLineSegment(sketch, "E897.MirrorCS", {"start": v(-119.43, 27.65) * mm, "end": v(-119.44, 28.62) * mm});
            skLineSegment(sketch, "E898.MirrorCS", {"start": v(-119.4, 24.07) * mm, "end": v(-119.4, 23.6) * mm});
            skLineSegment(sketch, "E899.MirrorCS", {"start": v(-119.4, 23.6) * mm, "end": v(-119.39, 23.13) * mm});
            skArc(sketch, "E900", {"start": v(-119.61, 24.05) * mm, "mid": v(-119.6, 24.05) * mm, "end": v(-119.6, 24.05) * mm});
            skLineSegment(sketch, "E901.0", {"start": v(-122.15, 25.68) * mm, "end": v(-120.98, 25.68) * mm});
            skLineSegment(sketch, "E902.0", {"start": v(-122.15, 26.06) * mm, "end": v(-120.98, 26.06) * mm});
            skLineSegment(sketch, "E903.trimOffspring", {"start": v(-118.25, 26.07) * mm, "end": v(-117.08, 26.08) * mm});
            skPoint(sketch, "E904.orphan", {"position": v(-119.61, 25.87) * mm});
            skLineSegment(sketch, "E905.trimOffspring", {"start": v(-118.24, 25.7) * mm, "end": v(-117.08, 25.7) * mm});
            skPoint(sketch, "E906.MirrorCS.end.orphan", {"position": v(-119.6, 24.05) * mm});
            skPoint(sketch, "E906.MirrorCS.start.orphan", {"position": v(-119.4, 24.07) * mm});
            skPoint(sketch, "E907.MirrorCS.end.orphan", {"position": v(-119.22, 23.12) * mm});
            skPoint(sketch, "E907.MirrorCS.start.orphan", {"position": v(-119.01, 23.13) * mm});
            skPoint(sketch, "E908.orphan", {"position": v(-119.63, 28.62) * mm});
            skPoint(sketch, "E909.MirrorCS.end.orphan", {"position": v(-119.43, 27.65) * mm});
            skArc(sketch, "E910.trimOffspring", {"start": v(-122.15, 25.68) * mm, "mid": v(-122.13, 25.46) * mm, "end": v(-122.1, 25.25) * mm});
            skArc(sketch, "E911.trimOffspring", {"start": v(-120.98, 25.68) * mm, "mid": v(-120.95, 25.38) * mm, "end": v(-120.88, 25.08) * mm});
            skArc(sketch, "E912.trimOffspring", {"start": v(-118.24, 25.7) * mm, "mid": v(-118.28, 25.4) * mm, "end": v(-118.34, 25.1) * mm});
            skArc(sketch, "E913.trimOffspring", {"start": v(-117.08, 25.7) * mm, "mid": v(-117.1, 25.49) * mm, "end": v(-117.11, 25.27) * mm});
            skText(sketch, "E914", { "text": "X", "fontName": "OpenSans-Bold.ttf"});
            skLineSegment(sketch, "E915", {"start": v(-117.9, 19.74) * mm, "end": v(-117.9, 21) * mm});
            skLineSegment(sketch, "E916", {"start": v(-117.9, 21) * mm, "end": v(-117.9, 19.74) * mm});
            skCircle(sketch, "E917", {"center": v(-119.61, 25.87) * mm, "radius": 0.65 * mm});
            skArc(sketch, "E918.0", {"start": v(-117.9, 19.74) * mm, "mid": v(-122.2, 21.23) * mm, "end": v(-126.46, 19.59) * mm});
            skLineSegment(sketch, "E919", {"start": v(-126.46, 20.87) * mm, "end": v(-126.46, 19.59) * mm});
            skArc(sketch, "E920.MirrorCS", {"start": v(-146.07, -38.65) * mm, "mid": v(-145.9, -38.4) * mm, "end": v(-145.84, -38.12) * mm});
            skArc(sketch, "E921.MirrorCS", {"start": v(-144.31, -18.87) * mm, "mid": v(-145.08, -18.11) * mm, "end": v(-145.84, -18.87) * mm});
            skArc(sketch, "E922.MirrorCS", {"start": v(-146.92, -38.62) * mm, "mid": v(-146.5, -38.77) * mm, "end": v(-146.07, -38.65) * mm});
            skLineSegment(sketch, "E923.MirrorCS", {"start": v(-145.84, -39.38) * mm, "end": v(-145.84, -39.45) * mm});
            skArc(sketch, "E924.MirrorCS", {"start": v(-135.11, -16.25) * mm, "mid": v(-135.88, -15.5) * mm, "end": v(-136.65, -16.25) * mm});
            skArc(sketch, "E925.MirrorCS", {"start": v(-141.25, -17.83) * mm, "mid": v(-142.01, -17.07) * mm, "end": v(-142.78, -17.83) * mm});
            skArc(sketch, "E926.MirrorCS", {"start": v(-135.11, -39.45) * mm, "mid": v(-134.35, -40.2) * mm, "end": v(-133.58, -39.45) * mm});
            skArc(sketch, "E927.MirrorCS", {"start": v(-141.25, -39.45) * mm, "mid": v(-140.48, -40.2) * mm, "end": v(-139.71, -39.45) * mm});
            skArc(sketch, "E928.MirrorCS", {"start": v(-124.38, -14.8) * mm, "mid": v(-123.62, -14.05) * mm, "end": v(-122.85, -14.8) * mm});
            skLineSegment(sketch, "E929.MirrorCS", {"start": v(-142.78, -17.83) * mm, "end": v(-142.78, -39.4) * mm});
            skLineSegment(sketch, "E930.MirrorCS", {"start": v(-136.65, -16.25) * mm, "end": v(-136.65, -39.45) * mm});
            skLineSegment(sketch, "E931.MirrorCS", {"start": v(-130.52, -15.26) * mm, "end": v(-130.52, -39.45) * mm});
            skLineSegment(sketch, "E932.MirrorCS", {"start": v(-127.45, -14.95) * mm, "end": v(-127.45, -39.45) * mm});
            skLineSegment(sketch, "E933.MirrorCS", {"start": v(-122.85, -39.45) * mm, "end": v(-122.85, -14.8) * mm});
            skArc(sketch, "E934.MirrorCS", {"start": v(-132.05, -15.67) * mm, "mid": v(-132.82, -14.9) * mm, "end": v(-133.58, -15.67) * mm});
            skLineSegment(sketch, "E935.MirrorCS", {"start": v(-124.38, -14.8) * mm, "end": v(-124.38, -39.45) * mm});
            skLineSegment(sketch, "E936.MirrorCS", {"start": v(-144.31, -39.4) * mm, "end": v(-144.31, -18.87) * mm});
            skLineSegment(sketch, "E937.MirrorCS", {"start": v(-145.84, -18.87) * mm, "end": v(-145.84, -38.12) * mm});
            skArc(sketch, "E938.MirrorCS", {"start": v(-122.85, -14.8) * mm, "mid": v(-123.62, -14.05) * mm, "end": v(-124.38, -14.8) * mm});
            skLineSegment(sketch, "E939.MirrorCS", {"start": v(-133.58, -15.67) * mm, "end": v(-133.58, -39.45) * mm});
            skLineSegment(sketch, "E940.MirrorCS", {"start": v(-141.25, -39.45) * mm, "end": v(-141.25, -17.83) * mm});
            skArc(sketch, "E941.MirrorCS", {"start": v(-138.18, -39.45) * mm, "mid": v(-137.41, -40.2) * mm, "end": v(-136.65, -39.45) * mm});
            skLineSegment(sketch, "E942.MirrorCS", {"start": v(-135.11, -39.45) * mm, "end": v(-135.11, -16.25) * mm});
            skArc(sketch, "E943.MirrorCS", {"start": v(-128.98, -39.45) * mm, "mid": v(-128.22, -40.2) * mm, "end": v(-127.45, -39.45) * mm});
            skLineSegment(sketch, "E944.MirrorCS", {"start": v(-138.18, -39.45) * mm, "end": v(-138.18, -16.96) * mm});
            skArc(sketch, "E945.MirrorCS", {"start": v(-125.92, -39.45) * mm, "mid": v(-125.15, -40.2) * mm, "end": v(-124.38, -39.45) * mm});
            skLineSegment(sketch, "E946.MirrorCS", {"start": v(-132.05, -39.45) * mm, "end": v(-132.05, -15.67) * mm});
            skLineSegment(sketch, "E947.MirrorCS", {"start": v(-125.92, -39.45) * mm, "end": v(-125.92, -14.95) * mm});
            skLineSegment(sketch, "E948.MirrorCS", {"start": v(-128.98, -39.45) * mm, "end": v(-128.98, -15.26) * mm});
            skArc(sketch, "E949.MirrorCS", {"start": v(-125.92, -14.95) * mm, "mid": v(-126.68, -14.2) * mm, "end": v(-127.45, -14.95) * mm});
            skLineSegment(sketch, "E950.MirrorCS", {"start": v(-139.71, -16.96) * mm, "end": v(-139.71, -39.45) * mm});
            skArc(sketch, "E951.MirrorCS", {"start": v(-144.31, -39.4) * mm, "mid": v(-143.55, -40.15) * mm, "end": v(-142.78, -39.4) * mm});
            skArc(sketch, "E952.MirrorCS", {"start": v(-132.05, -39.45) * mm, "mid": v(-131.28, -40.2) * mm, "end": v(-130.52, -39.45) * mm});
            skArc(sketch, "E953.MirrorCS", {"start": v(-138.18, -16.96) * mm, "mid": v(-138.95, -16.2) * mm, "end": v(-139.71, -16.96) * mm});
            skArc(sketch, "E954.MirrorCS", {"start": v(-128.98, -15.26) * mm, "mid": v(-129.75, -14.5) * mm, "end": v(-130.52, -15.26) * mm});
            skPoint(sketch, "E955.MirrorP", {"position": v(-147.78, -40.82) * mm});
            skLineSegment(sketch, "E956", {"start": v(-122.09, 45.4) * mm, "end": v(-122.09, -72.18) * mm, "construction": true});
            skArc(sketch, "E957.MirrorCS", {"start": v(-102.92, -39.45) * mm, "mid": v(-103.7, -40.2) * mm, "end": v(-104.46, -39.45) * mm});
            skArc(sketch, "E958.MirrorCS", {"start": v(-109.06, -39.45) * mm, "mid": v(-109.82, -40.2) * mm, "end": v(-110.59, -39.45) * mm});
            skArc(sketch, "E959.MirrorCS", {"start": v(-121.32, -14.8) * mm, "mid": v(-120.55, -14.05) * mm, "end": v(-119.79, -14.8) * mm});
            skArc(sketch, "E960.MirrorCS", {"start": v(-106, -39.45) * mm, "mid": v(-106.76, -40.2) * mm, "end": v(-107.52, -39.45) * mm});
            skLineSegment(sketch, "E961.MirrorCS", {"start": v(-108.54, 24.43) * mm, "end": v(-108.55, 24.43) * mm});
            skArc(sketch, "E962.MirrorCS", {"start": v(-119.79, -14.8) * mm, "mid": v(-120.55, -14.05) * mm, "end": v(-121.32, -14.8) * mm});
            skLineSegment(sketch, "E963.MirrorCS", {"start": v(-98.33, -39.38) * mm, "end": v(-98.33, -39.45) * mm});
            skArc(sketch, "E964.MirrorCS", {"start": v(-95.1, 12.99) * mm, "mid": v(-95.85, 13.75) * mm, "end": v(-95.1, 14.52) * mm});
            skArc(sketch, "E965.MirrorCS", {"start": v(-95.1, 22.18) * mm, "mid": v(-95.85, 22.95) * mm, "end": v(-95.1, 23.71) * mm});
            skLineSegment(sketch, "E966.MirrorCS", {"start": v(-95.1, 25.25) * mm, "end": v(-95.1, 23.71) * mm});
            skArc(sketch, "E967.MirrorCS", {"start": v(-98.1, -38.65) * mm, "mid": v(-98.27, -38.4) * mm, "end": v(-98.33, -38.12) * mm});
            skArc(sketch, "E968.MirrorCS", {"start": v(-118.25, -39.45) * mm, "mid": v(-119.02, -40.2) * mm, "end": v(-119.79, -39.45) * mm});
            skLineSegment(sketch, "E969.MirrorCS", {"start": v(-95.1, 28.31) * mm, "end": v(-95.1, 26.78) * mm});
            skArc(sketch, "E970.MirrorCS", {"start": v(-106.78, 24.42) * mm, "mid": v(-107.17, 24.63) * mm, "end": v(-107.34, 25.04) * mm});
            skArc(sketch, "E971.MirrorCS", {"start": v(-95.1, 34.44) * mm, "mid": v(-95.85, 35.21) * mm, "end": v(-95.1, 35.98) * mm});
            skLineSegment(sketch, "E972.MirrorCS", {"start": v(-95.1, 31.38) * mm, "end": v(-95.1, 29.85) * mm});
            skArc(sketch, "E973.MirrorCS", {"start": v(-108.79, 24.42) * mm, "mid": v(-108.4, 24.63) * mm, "end": v(-108.23, 25.04) * mm});
            skArc(sketch, "E974.MirrorCS", {"start": v(-113.69, 36.12) * mm, "mid": v(-113.7, 35.92) * mm, "end": v(-113.84, 35.8) * mm});
            skArc(sketch, "E975.MirrorCS", {"start": v(-95.1, 31.38) * mm, "mid": v(-95.85, 32.15) * mm, "end": v(-95.1, 32.91) * mm});
            skArc(sketch, "E976.MirrorCS", {"start": v(-95.1, 25.25) * mm, "mid": v(-95.85, 26.01) * mm, "end": v(-95.1, 26.78) * mm});
            skLineSegment(sketch, "E977.MirrorCS", {"start": v(-95.1, 34.44) * mm, "end": v(-95.1, 32.91) * mm});
            skArc(sketch, "E978.MirrorCS", {"start": v(-99.86, -39.4) * mm, "mid": v(-100.63, -40.15) * mm, "end": v(-101.4, -39.4) * mm});
            skArc(sketch, "E979.MirrorCS", {"start": v(-95.1, 28.31) * mm, "mid": v(-95.85, 29.08) * mm, "end": v(-95.1, 29.85) * mm});
            skLineSegment(sketch, "E980.MirrorCS", {"start": v(-95.1, 12.99) * mm, "end": v(-95.1, 11.45) * mm});
            skLineSegment(sketch, "E981.MirrorCS", {"start": v(-109.19, 40.63) * mm, "end": v(-109.37, 40.63) * mm});
            skArc(sketch, "E982.MirrorCS", {"start": v(-97.25, -38.62) * mm, "mid": v(-97.67, -38.77) * mm, "end": v(-98.1, -38.65) * mm});
            skArc(sketch, "E983.MirrorCS", {"start": v(-115.19, -39.45) * mm, "mid": v(-115.95, -40.2) * mm, "end": v(-116.72, -39.45) * mm});
            skArc(sketch, "E984.MirrorCS", {"start": v(-102.92, -17.83) * mm, "mid": v(-102.16, -17.07) * mm, "end": v(-101.4, -17.83) * mm});
            skLineSegment(sketch, "E985.MirrorCS", {"start": v(-95.1, 16.05) * mm, "end": v(-95.1, 14.52) * mm});
            skLineSegment(sketch, "E986.MirrorCS", {"start": v(-106.2, 40.63) * mm, "end": v(-106.4, 40.63) * mm});
            skArc(sketch, "E987.MirrorCS", {"start": v(-95.1, 9.92) * mm, "mid": v(-95.85, 10.69) * mm, "end": v(-95.1, 11.45) * mm});
            skArc(sketch, "E988.MirrorCS", {"start": v(-109.06, -16.25) * mm, "mid": v(-108.29, -15.5) * mm, "end": v(-107.52, -16.25) * mm});
            skArc(sketch, "E989.MirrorCS", {"start": v(-95.1, 19.12) * mm, "mid": v(-95.85, 19.88) * mm, "end": v(-95.1, 20.65) * mm});
            skLineSegment(sketch, "E990.MirrorCS", {"start": v(-95.1, 37.51) * mm, "end": v(-95.1, 35.98) * mm});
            skLineSegment(sketch, "E991.MirrorCS", {"start": v(-95.1, 22.18) * mm, "end": v(-95.1, 20.65) * mm});
            skArc(sketch, "E992.MirrorCS", {"start": v(-115.19, -15.26) * mm, "mid": v(-114.42, -14.5) * mm, "end": v(-113.65, -15.26) * mm});
            skLineSegment(sketch, "E993.MirrorCS", {"start": v(-95.1, 19.12) * mm, "end": v(-95.1, 17.58) * mm});
            skArc(sketch, "E994.MirrorCS", {"start": v(-112.12, -39.45) * mm, "mid": v(-112.89, -40.2) * mm, "end": v(-113.65, -39.45) * mm});
            skLineSegment(sketch, "E995.MirrorCS", {"start": v(-108.23, 35.86) * mm, "end": v(-107.34, 35.86) * mm});
            skArc(sketch, "E996.MirrorCS", {"start": v(-95.1, 16.05) * mm, "mid": v(-95.85, 16.82) * mm, "end": v(-95.1, 17.58) * mm});
            skLineSegment(sketch, "E997.MirrorCS", {"start": v(-107.02, 28.2) * mm, "end": v(-107.02, 28.19) * mm});
            skArc(sketch, "E998.MirrorCS", {"start": v(-101.15, 2.98) * mm, "mid": v(-99.74, 3.8) * mm, "end": v(-98.24, 4.43) * mm});
            skArc(sketch, "E999.MirrorCS", {"start": v(-118.25, -14.95) * mm, "mid": v(-117.49, -14.2) * mm, "end": v(-116.72, -14.95) * mm});
            skLineSegment(sketch, "E1000.MirrorCS", {"start": v(-113.8, 39.04) * mm, "end": v(-117.32, 39.04) * mm});
            skLineSegment(sketch, "E1001.MirrorCS", {"start": v(-108.55, 28.2) * mm, "end": v(-108.55, 28.2) * mm});
            skLineSegment(sketch, "E1002.MirrorCS", {"start": v(-117.32, 40.63) * mm, "end": v(-117.32, 39.04) * mm});
            skArc(sketch, "E1003.MirrorCS", {"start": v(-95.1, 37.51) * mm, "mid": v(-95.85, 38.28) * mm, "end": v(-95.1, 39.04) * mm});
            skArc(sketch, "E1004.MirrorCS", {"start": v(-113.69, 36.12) * mm, "mid": v(-114.06, 37.57) * mm, "end": v(-113.8, 39.04) * mm});
            skArc(sketch, "E1005.MirrorCS", {"start": v(-106.4, 40.63) * mm, "mid": v(-107.8, 41.44) * mm, "end": v(-109.19, 40.63) * mm});
            skLineSegment(sketch, "E1006.MirrorCS", {"start": v(-109.19, 39.04) * mm, "end": v(-112.8, 39.04) * mm});
            skArc(sketch, "E1007.MirrorCS", {"start": v(-106, -16.96) * mm, "mid": v(-105.22, -16.2) * mm, "end": v(-104.46, -16.96) * mm});
            skLineSegment(sketch, "E1008.MirrorCS", {"start": v(-95.1, 8.6) * mm, "end": v(-95.1, 9.92) * mm});
            skArc(sketch, "E1009.MirrorCS", {"start": v(-112.12, -15.67) * mm, "mid": v(-111.36, -14.9) * mm, "end": v(-110.59, -15.67) * mm});
            skLineSegment(sketch, "E1010.MirrorCS", {"start": v(-96.9, -4.6) * mm, "end": v(-95.1, -4.6) * mm});
            skArc(sketch, "E1011.MirrorCS", {"start": v(-112.18, 35.64) * mm, "mid": v(-113.13, 37.22) * mm, "end": v(-112.8, 39.04) * mm});
            skArc(sketch, "E1012.MirrorCS", {"start": v(-109.19, 39.04) * mm, "mid": v(-107.8, 38.24) * mm, "end": v(-106.4, 39.04) * mm});
            skArc(sketch, "E1013.MirrorCS", {"start": v(-99.86, -18.87) * mm, "mid": v(-99.1, -18.11) * mm, "end": v(-98.33, -18.87) * mm});
            skLineSegment(sketch, "E1014.MirrorCS", {"start": v(-98.27, 39.04) * mm, "end": v(-98.27, 40.63) * mm});
            skLineSegment(sketch, "E1015.MirrorCS", {"start": v(-101.4, -17.83) * mm, "end": v(-101.4, -39.4) * mm});
            skPoint(sketch, "E1016.MirrorP", {"position": v(-112.15, 35.61) * mm});
            skArc(sketch, "E1017.MirrorCS", {"start": v(-112.18, 35.64) * mm, "mid": v(-113.5, 30.6) * mm, "end": v(-113.84, 35.8) * mm});
            skLineSegment(sketch, "E1018.MirrorCS", {"start": v(-101.45, 45.4) * mm, "end": v(-142.72, 45.4) * mm});
            skLineSegment(sketch, "E1019.MirrorCS", {"start": v(-116.72, -14.95) * mm, "end": v(-116.72, -39.45) * mm});
            skLineSegment(sketch, "E1020.MirrorCS", {"start": v(-98.27, 40.63) * mm, "end": v(-106.2, 40.63) * mm});
            skLineSegment(sketch, "E1021.MirrorCS", {"start": v(-98.33, -18.87) * mm, "end": v(-98.33, -38.12) * mm});
            skArc(sketch, "E1022.MirrorCS", {"start": v(-95.1, 8.6) * mm, "mid": v(-95.98, 6) * mm, "end": v(-98.24, 4.43) * mm});
            skLineSegment(sketch, "E1023.MirrorCS", {"start": v(-107.34, 35.86) * mm, "end": v(-107.34, 25.04) * mm});
            skLineSegment(sketch, "E1024.MirrorCS", {"start": v(-95.1, -4.6) * mm, "end": v(-95.13, -34.52) * mm});
            skLineSegment(sketch, "E1025.MirrorCS", {"start": v(-104.46, -16.96) * mm, "end": v(-104.46, -39.45) * mm});
            skLineSegment(sketch, "E1026.MirrorCS", {"start": v(-109.06, -39.45) * mm, "end": v(-109.06, -16.25) * mm});
            skArc(sketch, "E1027.MirrorCS", {"start": v(-101.45, 45.4) * mm, "mid": v(-96.96, 43.53) * mm, "end": v(-95.1, 39.04) * mm});
            skPoint(sketch, "E1028.MirrorP", {"position": v(-107.78, 35.86) * mm});
            skLineSegment(sketch, "E1029.MirrorCS", {"start": v(-115.19, -39.45) * mm, "end": v(-115.19, -15.26) * mm});
            skLineSegment(sketch, "E1030.MirrorCS", {"start": v(-110.59, -15.67) * mm, "end": v(-110.59, -39.45) * mm});
            skLineSegment(sketch, "E1031.MirrorCS", {"start": v(-98.27, 39.04) * mm, "end": v(-106.4, 39.04) * mm});
            skLineSegment(sketch, "E1032.MirrorCS", {"start": v(-99.86, -39.4) * mm, "end": v(-99.86, -18.87) * mm});
            skArc(sketch, "E1033.MirrorCS", {"start": v(-106.78, 24.42) * mm, "mid": v(-107.8, 11.66) * mm, "end": v(-108.77, 24.42) * mm});
            skLineSegment(sketch, "E1034.MirrorCS", {"start": v(-107.52, -16.25) * mm, "end": v(-107.52, -39.45) * mm});
            skArc(sketch, "E1035.MirrorCS", {"start": v(-96.9, -4.6) * mm, "mid": v(-99.34, -9.6) * mm, "end": v(-104.17, -6.86) * mm});
            skLineSegment(sketch, "E1036.MirrorCS", {"start": v(-118.25, -39.45) * mm, "end": v(-118.25, -14.95) * mm});
            skLineSegment(sketch, "E1037.MirrorCS", {"start": v(-102.92, -39.45) * mm, "end": v(-102.92, -17.83) * mm});
            skLineSegment(sketch, "E1038.MirrorCS", {"start": v(-112.12, -39.45) * mm, "end": v(-112.12, -15.67) * mm});
            skPoint(sketch, "E1039.MirrorP", {"position": v(-96.39, -40.82) * mm});
            skPoint(sketch, "E1040.MirrorP", {"position": v(-112.18, 35.64) * mm});
            skLineSegment(sketch, "E1041.MirrorCS", {"start": v(-109.37, 40.63) * mm, "end": v(-117.32, 40.63) * mm});
            skArc(sketch, "E1042.MirrorCS", {"start": v(-95.13, -34.52) * mm, "mid": v(-95.8, -36.77) * mm, "end": v(-97.25, -38.62) * mm});
            skArc(sketch, "E1043.MirrorCS", {"start": v(-104.17, -6.86) * mm, "mid": v(-104.15, -1.48) * mm, "end": v(-101.15, 2.98) * mm});
            skLineSegment(sketch, "E1044.MirrorCS", {"start": v(-113.65, -15.26) * mm, "end": v(-113.65, -39.45) * mm});
            skLineSegment(sketch, "E1045.MirrorCS", {"start": v(-108.23, 35.86) * mm, "end": v(-108.23, 25.04) * mm});
            skLineSegment(sketch, "E1046.MirrorCS", {"start": v(-121.32, -39.45) * mm, "end": v(-121.32, -14.8) * mm});
            skLineSegment(sketch, "E1047.MirrorCS", {"start": v(-106, -39.45) * mm, "end": v(-106, -16.96) * mm});
            skLineSegment(sketch, "E1048.MirrorCS", {"start": v(-119.79, -14.8) * mm, "end": v(-119.79, -39.45) * mm});
            skLineSegment(sketch, "E1049", {"start": v(-149.05, -13.59) * mm, "end": v(-149.04, -34.52) * mm});
            const initialGuessF0  = {"E244": [-0.00542, 0.02332, 1, 0, 0.005], "E495": [0.0546, 0.02332, 1, 0, 0.005], "E739": [-0.06565, 0.02394, 1, 0, 0.005], "E914": [-0.12762, 0.0235, 1, 0, 0.005]};
            skSetInitialGuess(sketch, initialGuessF0);
            skSolve(sketch);
        }
        {
            var Q0;
            Q0=makeQuery(id+"F0.imprint","IMPRINT",FACE,{"disambiguationData":[TD([[makeQuery(id+"F0.imprint","IMPRINT",EDGE,{"derivedFrom":sQuery(id+"F0.wireOp",EDGE,"E251.0")}),1.0]])]});
            var Q1;
            Q1=makeQuery(id+"F0.imprint","IMPRINT",FACE,{"disambiguationData":[TD([[makeQuery(id+"F0.imprint","IMPRINT",EDGE,{"derivedFrom":sQuery(id+"F0.wireOp",EDGE,"E0.0")}),1.0]])]});
            var Q2;
            Q2=makeQuery(id+"F0.imprint","IMPRINT",FACE,{"disambiguationData":[TD([[makeQuery(id+"F0.imprint","IMPRINT",EDGE,{"derivedFrom":sQuery(id+"F0.wireOp",EDGE,"E529.0")}),1.0]])]});
            var Q3;
            Q3=makeQuery(id+"F0.imprint","IMPRINT",FACE,{"disambiguationData":[TD([[makeQuery(id+"F0.imprint","IMPRINT",EDGE,{"derivedFrom":sQuery(id+"F0.wireOp",EDGE,"E793.left")}),1.0]])]});
            extrude(context, id + "F1", {"entities" : qUnion([Q0, Q1, Q2, Q3]), "oppositeDirection" : true, "depth" : 3.17 * mm, "offsetDistance" : 25.4 * mm});
        }
        {
            var Q0;
            Q0=makeQuery(id+"F1.opExtrude","CAP_EDGE",EDGE,{"disambiguationData":[OSD([sQuery(id+"F0.wireOp",EDGE,"E795.filletArc")])],"isStart":true});
            var Q1;
            Q1=makeQuery(id+"F1.opExtrude","CAP_EDGE",EDGE,{"disambiguationData":[OSD([sQuery(id+"F0.wireOp",EDGE,"E847.MirrorCS"),sQuery(id+"F0.wireOp",EDGE,"E1049")])],"isStart":true});
            chamfer(context, id + "F2", {"entities" : qUnion([Q0, Q1]), "width" : 3.17 * mm});
        }
    });
